# Revit family: d0086212_REVIT-TP96
name_source: partatom
category: Mechanical Equipment
revit_build: Autodesk Revit 2017 (Build: 20190507_1515(x64)
units: mm (PartAtom-declared; Revit-internal decimal feet)

## family parameters
Always vertical = Yes
Cut with Voids When Loaded = Yes
Part Type = Normal
Room Calculation Point = No
Round Connector Dimension = Use Radius
Shared = No
Work Plane-Based = No

## types (50) — shared parameters
Air Inlet Radius = 3 5/16"
Assembly Code = D3020100
Burner Housing Y = 3 13/16"
Burner Nozzle Radius = 2 5/8"
Combustion Air Connection = 6 5/8"
Combustion Air Connection Extension = 5 13/16"
Combustion Air Inlet Radius = 3 5/16"
Condensate Connection = 3/4"
Condensate Drain Extension = 12"
Condensate Location = 4"
Condensate Outlet Extension = 15 1/4"
Condensate Radius = 3/8"
Control Enclosure Height = 38"
Control Enclosure Width = 12"
Cowling Radius = 14 5/8"
Description = TURBOPOWER® 96 ▪ CONDENSING GAS WATER HEATER
Disclaimer = This rendering is for building modeling purposes only. Submittal/catalog is still the contract document. PVI reserves the right to change design and specification without notice.
Drain Angle = 90.00°
Drain Height = 4 3/8"
Economizer Height = 12 3/8"
Flue Collector Insert Radius = 7 9/16"
Flue Collector Outlet Extension = 7 5/8"
Flue Collector Outlet Radius = 3 3/8"
Gas Train Height = 14 7/8"
Gas Train Location = 9 1/4"
Manufacturer = PVI Industries, LLC
Skid Height = 5"
Tank Building Outlet = 18 3/16"
URL = www.pvi.com
Vent Connection = 6 5/8"
Vent Connection Height = 2 3/4"
Vent Enclosure Height = 4"
Vent Radius = 3 5/16"

## per-type parameters (varying)
- 50 L 250A-TPX: 100 Prefix Recovery Rate 40F to 140F (gph)=-; 130 Prefix Recovery Rate 40F to 140F (gph)=-; 160 Prefix Recovery Rate 40F to 140F (gph)=-; 50 Prefix Recovery Rate 40F to 140F (gph)=587; 75 Prefix Recovery Rate 40F to 140F (gph)=-; Building Return Connection Height 50 (250-400gal only) prefix=14 3/16"; Building Return Connection Height 50-160 prefix=10 1/2"; Building Return Extension 250-400gal=35 7/8"; Building Return Extension 500-600gal=5"; Building Return Extension Angle 500-600gal=45.00°; Building Return Height=18 3/16"; Building Return Location=25 3/8"; Building Return NPT=1 1/2"; Building Return Radius=3/4"; Building Return to Economizer=7 5/8"; Burner Conn Height=57 7/8"; Burner Height=18"; Burner Housing -Y=15 5/8"; Burner Housing Extension=19"; Burner Housing to Left=5 3/16"; Burner Housing to Right=7 1/4"; Burner Nozzle Extension=12 3/8"; Cold Inlet Extension=34"; Cold Inlet NPT=2"; Cold Inlet Radius=1"; Combustion Air Connection X=15 7/16"; Combustion Air Connection to Right=3 9/16"; Condensate Extension=4 3/8"; Control Enclosure Angle=56.00°; Control Enclosure Location=41 5/16"; Control Panel Extension=30"; Drain Extension=24 5/8"; Drain NPT=1"; Drain Radius=1/2"; Economizer Connection Y=5"; Economizer Depth=10"; Economizer Inlet Outlet Connection Spacing=4"; Economizer Width=32"; Energy Height=30 7/8"; Flue Collector Extension=8 13/16"; Flue Collector Outlet to Front=3 11/16"; Flue Collector Radius=12 1/8"; Front Cowling Extension=31 1/4"; Gas Inlet NPT=1"; Gas Inlet Radius=1/2"; Gas Train Extension=17 3/8"; Gas Train To Front=10 11/16"; Gas Train Vertical=19 1/8"; Gas Train to Left=4 3/8"; Gas Train to Rear=9 11/16"; Height to Cold Inlet=19 7/16"; Height to Hot Outlet 400-1500gal=45"; Hot Outlet Angle=90.00°; Hot Outlet Extension=24"; Hot Outlet Radius=1"; Hot Outlet Side 400-1500gal NPT=0"; Hot Outlet Side Extension=24"; Hot Outlet Top 250-400gal NPT=2"; Input=500000 Btu/h; Model=50 L 250A-TPX; Pump Extension=27 3/8"; Pump Line Radius=5/8"; Pump Line to Economizer Location=29 3/4"; Rear Cowling Extension=1"; Relief Angle 50-160 Prefix=45.00°; Relief Angle 75-160 Prefix=30.00°; Relief Extension=27"; Relief Extension 50-160 Prefix=27"; Relief Extension 75-160 Prefix=5"; Relief Height=47"; Relief NPT=3/4"; Relief Radius=3/8"; Shipping Weight lbs.=1710; Skid Length=72 1/2"; Skid Spacing=28"; Skid to Front=44 13/16"; Test Building Return Height=16"; Unit Height=62 7/8"; Unit Radius=23"; Vent Connection Housing Extension=8 13/16"; Vent Extension=26 3/8"; Vent Height=7 1/4"; Vent Location=5 3/8"
- 50 L 300A-TPX: 100 Prefix Recovery Rate 40F to 140F (gph)=-; 130 Prefix Recovery Rate 40F to 140F (gph)=-; 160 Prefix Recovery Rate 40F to 140F (gph)=-; 50 Prefix Recovery Rate 40F to 140F (gph)=587; 75 Prefix Recovery Rate 40F to 140F (gph)=-; Building Return Connection Height 50 (250-400gal only) prefix=14 3/16"; Building Return Connection Height 50-160 prefix=10 1/2"; Building Return Extension 250-400gal=35 7/8"; Building Return Extension 500-600gal=5"; Building Return Extension Angle 500-600gal=45.00°; Building Return Height=18 3/16"; Building Return Location=25 3/8"; Building Return NPT=1 1/2"; Building Return Radius=3/4"; Building Return to Economizer=7 5/8"; Burner Conn Height=69 7/8"; Burner Height=18"; Burner Housing -Y=15 5/8"; Burner Housing Extension=19"; Burner Housing to Left=5 3/16"; Burner Housing to Right=7 1/4"; Burner Nozzle Extension=12 3/8"; Cold Inlet Extension=34"; Cold Inlet NPT=2"; Cold Inlet Radius=1"; Combustion Air Connection X=15 7/16"; Combustion Air Connection to Right=3 9/16"; Condensate Extension=4 3/8"; Control Enclosure Angle=56.00°; Control Enclosure Location=51 1/4"; Control Panel Extension=30"; Drain Extension=24 5/8"; Drain NPT=1"; Drain Radius=1/2"; Economizer Connection Y=5"; Economizer Depth=10"; Economizer Inlet Outlet Connection Spacing=4"; Economizer Width=32"; Energy Height=30 7/8"; Flue Collector Extension=8 13/16"; Flue Collector Outlet to Front=3 11/16"; Flue Collector Radius=12 1/8"; Front Cowling Extension=31 1/4"; Gas Inlet NPT=1"; Gas Inlet Radius=1/2"; Gas Train Extension=17 3/8"; Gas Train To Front=10 11/16"; Gas Train Vertical=19 1/8"; Gas Train to Left=4 3/8"; Gas Train to Rear=9 11/16"; Height to Cold Inlet=19 7/16"; Height to Hot Outlet 400-1500gal=57"; Hot Outlet Angle=90.00°; Hot Outlet Extension=24"; Hot Outlet Radius=1"; Hot Outlet Side 400-1500gal NPT=0"; Hot Outlet Side Extension=24"; Hot Outlet Top 250-400gal NPT=2"; Input=500000 Btu/h; Model=50 L 300A-TPX; Pump Extension=27 3/8"; Pump Line Radius=5/8"; Pump Line to Economizer Location=29 3/4"; Rear Cowling Extension=1"; Relief Angle 50-160 Prefix=45.00°; Relief Angle 75-160 Prefix=30.00°; Relief Extension=27"; Relief Extension 50-160 Prefix=27"; Relief Extension 75-160 Prefix=5"; Relief Height=59"; Relief NPT=3/4"; Relief Radius=3/8"; Shipping Weight lbs.=1770; Skid Length=72 1/2"; Skid Spacing=28"; Skid to Front=44 13/16"; Test Building Return Height=16 3/16"; Unit Height=74 7/8"; Unit Radius=23"; Vent Connection Housing Extension=8 13/16"; Vent Extension=26 3/8"; Vent Height=7 1/4"; Vent Location=5 3/8"
- 50 L 400A-TPX: 100 Prefix Recovery Rate 40F to 140F (gph)=-; 130 Prefix Recovery Rate 40F to 140F (gph)=-; 160 Prefix Recovery Rate 40F to 140F (gph)=-; 50 Prefix Recovery Rate 40F to 140F (gph)=587; 75 Prefix Recovery Rate 40F to 140F (gph)=-; Building Return Connection Height 50 (250-400gal only) prefix=14 3/16"; Building Return Connection Height 50-160 prefix=10 1/2"; Building Return Extension 250-400gal=35 7/8"; Building Return Extension 500-600gal=5"; Building Return Extension Angle 500-600gal=45.00°; Building Return Height=18 3/16"; Building Return Location=25 3/8"; Building Return NPT=1 1/2"; Building Return Radius=3/4"; Building Return to Economizer=7 5/8"; Burner Conn Height=81 7/8"; Burner Height=18"; Burner Housing -Y=15 5/8"; Burner Housing Extension=19"; Burner Housing to Left=5 3/16"; Burner Housing to Right=7 1/4"; Burner Nozzle Extension=12 3/8"; Cold Inlet Extension=34"; Cold Inlet NPT=2"; Cold Inlet Radius=1"; Combustion Air Connection X=15 7/16"; Combustion Air Connection to Right=3 9/16"; Condensate Extension=4 3/8"; Control Enclosure Angle=56.00°; Control Enclosure Location=51 1/4"; Control Panel Extension=30"; Drain Extension=24 5/8"; Drain NPT=1"; Drain Radius=1/2"; Economizer Connection Y=5"; Economizer Depth=10"; Economizer Inlet Outlet Connection Spacing=4"; Economizer Width=32"; Energy Height=30 7/8"; Flue Collector Extension=8 13/16"; Flue Collector Outlet to Front=3 11/16"; Flue Collector Radius=12 1/8"; Front Cowling Extension=31 1/4"; Gas Inlet NPT=1"; Gas Inlet Radius=1/2"; Gas Train Extension=17 3/8"; Gas Train To Front=10 11/16"; Gas Train Vertical=19 1/8"; Gas Train to Left=4 3/8"; Gas Train to Rear=9 11/16"; Height to Cold Inlet=19 7/16"; Height to Hot Outlet 400-1500gal=73 1/2"; Hot Outlet Angle=0.00°; Hot Outlet Extension=24"; Hot Outlet Radius=1"; Hot Outlet Side 400-1500gal NPT=0"; Hot Outlet Side Extension=24"; Hot Outlet Top 250-400gal NPT=2"; Input=500000 Btu/h; Model=50 L 400A-TPX; Pump Extension=27 3/8"; Pump Line Radius=5/8"; Pump Line to Economizer Location=29 3/4"; Rear Cowling Extension=1"; Relief Angle 50-160 Prefix=45.00°; Relief Angle 75-160 Prefix=30.00°; Relief Extension=27"; Relief Extension 50-160 Prefix=27"; Relief Extension 75-160 Prefix=5"; Relief Height=71"; Relief NPT=3/4"; Relief Radius=3/8"; Shipping Weight lbs.=1805; Skid Length=72 1/2"; Skid Spacing=28"; Skid to Front=44 13/16"; Test Building Return Height=16 3/16"; Unit Height=86 7/8"; Unit Radius=23"; Vent Connection Housing Extension=8 13/16"; Vent Extension=26 3/8"; Vent Height=7 1/4"; Vent Location=5 3/8"
- 75 L 250A-TPX: 100 Prefix Recovery Rate 40F to 140F (gph)=-; 130 Prefix Recovery Rate 40F to 140F (gph)=-; 160 Prefix Recovery Rate 40F to 140F (gph)=-; 50 Prefix Recovery Rate 40F to 140F (gph)=-; 75 Prefix Recovery Rate 40F to 140F (gph)=881; Building Return Connection Height 50 (250-400gal only) prefix=1/2"; Building Return Connection Height 50-160 prefix=14 3/16"; Building Return Extension 250-400gal=40 3/8"; Building Return Extension 500-600gal=5"; Building Return Extension Angle 500-600gal=45.00°; Building Return Height=18 3/16"; Building Return Location=28 1/2"; Building Return NPT=1 1/2"; Building Return Radius=3/4"; Building Return to Economizer=10 7/16"; Burner Conn Height=57 7/8"; Burner Height=18"; Burner Housing -Y=18 7/16"; Burner Housing Extension=20"; Burner Housing to Left=7 1/8"; Burner Housing to Right=7 7/8"; Burner Nozzle Extension=12 3/8"; Cold Inlet Extension=35 1/2"; Cold Inlet NPT=2"; Cold Inlet Radius=1"; Combustion Air Connection X=15 7/16"; Combustion Air Connection to Right=3 9/16"; Condensate Extension=4 3/8"; Control Enclosure Angle=56.00°; Control Enclosure Location=41 5/16"; Control Panel Extension=30"; Drain Extension=24 5/8"; Drain NPT=1"; Drain Radius=1/2"; Economizer Connection Y=5"; Economizer Depth=10"; Economizer Inlet Outlet Connection Spacing=4"; Economizer Width=32"; Energy Height=30 7/8"; Flue Collector Extension=8 13/16"; Flue Collector Outlet to Front=3 11/16"; Flue Collector Radius=12 1/8"; Front Cowling Extension=37 1/4"; Gas Inlet NPT=1"; Gas Inlet Radius=1/2"; Gas Train Extension=17 3/8"; Gas Train To Front=11 5/8"; Gas Train Vertical=20 5/8"; Gas Train to Left=4 3/8"; Gas Train to Rear=10 11/16"; Height to Cold Inlet=19 7/16"; Height to Hot Outlet 400-1500gal=45"; Hot Outlet Angle=90.00°; Hot Outlet Extension=24"; Hot Outlet Radius=1"; Hot Outlet Side 400-1500gal NPT=0"; Hot Outlet Side Extension=24"; Hot Outlet Top 250-400gal NPT=2"; Input=750000 Btu/h; Model=75 L 250A-TPX; Pump Extension=27 3/8"; Pump Line Radius=5/8"; Pump Line to Economizer Location=31 11/16"; Rear Cowling Extension=1"; Relief Angle 50-160 Prefix=45.00°; Relief Angle 75-160 Prefix=30.00°; Relief Extension=27"; Relief Extension 50-160 Prefix=27"; Relief Extension 75-160 Prefix=29"; Relief Height=47"; Relief NPT=3/4"; Relief Radius=3/8"; Shipping Weight lbs.=1830; Skid Length=78 3/4"; Skid Spacing=28"; Skid to Front=51 1/16"; Test Building Return Height=16 3/16"; Unit Height=62 7/8"; Unit Radius=23"; Vent Connection Housing Extension=8 13/16"; Vent Extension=26 3/8"; Vent Height=7 1/4"; Vent Location=5 3/8"
- 75 L 300A-TPX: 100 Prefix Recovery Rate 40F to 140F (gph)=-; 130 Prefix Recovery Rate 40F to 140F (gph)=-; 160 Prefix Recovery Rate 40F to 140F (gph)=-; 50 Prefix Recovery Rate 40F to 140F (gph)=-; 75 Prefix Recovery Rate 40F to 140F (gph)=881; Building Return Connection Height 50 (250-400gal only) prefix=1/2"; Building Return Connection Height 50-160 prefix=14 3/16"; Building Return Extension 250-400gal=40 3/8"; Building Return Extension 500-600gal=5"; Building Return Extension Angle 500-600gal=45.00°; Building Return Height=18 3/16"; Building Return Location=28 1/2"; Building Return NPT=1 1/2"; Building Return Radius=3/4"; Building Return to Economizer=10 7/16"; Burner Conn Height=69 7/8"; Burner Height=18"; Burner Housing -Y=18 7/16"; Burner Housing Extension=20"; Burner Housing to Left=7 1/8"; Burner Housing to Right=7 7/8"; Burner Nozzle Extension=12 3/8"; Cold Inlet Extension=35 1/2"; Cold Inlet NPT=2"; Cold Inlet Radius=1"; Combustion Air Connection X=15 7/16"; Combustion Air Connection to Right=3 9/16"; Condensate Extension=4 3/8"; Control Enclosure Angle=56.00°; Control Enclosure Location=51 1/4"; Control Panel Extension=30"; Drain Extension=24 5/8"; Drain NPT=1"; Drain Radius=1/2"; Economizer Connection Y=5"; Economizer Depth=10"; Economizer Inlet Outlet Connection Spacing=4"; Economizer Width=32"; Energy Height=30 7/8"; Flue Collector Extension=8 13/16"; Flue Collector Outlet to Front=3 11/16"; Flue Collector Radius=12 1/8"; Front Cowling Extension=37 1/4"; Gas Inlet NPT=1"; Gas Inlet Radius=1/2"; Gas Train Extension=17 3/8"; Gas Train To Front=11 5/8"; Gas Train Vertical=20 5/8"; Gas Train to Left=4 3/8"; Gas Train to Rear=10 11/16"; Height to Cold Inlet=19 7/16"; Height to Hot Outlet 400-1500gal=57"; Hot Outlet Angle=90.00°; Hot Outlet Extension=24"; Hot Outlet Radius=1"; Hot Outlet Side 400-1500gal NPT=0"; Hot Outlet Side Extension=24"; Hot Outlet Top 250-400gal NPT=2"; Input=750000 Btu/h; Model=75 L 300A-TPX; Pump Extension=27 3/8"; Pump Line Radius=5/8"; Pump Line to Economizer Location=31 11/16"; Rear Cowling Extension=1"; Relief Angle 50-160 Prefix=45.00°; Relief Angle 75-160 Prefix=30.00°; Relief Extension=27"; Relief Extension 50-160 Prefix=27"; Relief Extension 75-160 Prefix=29"; Relief Height=59"; Relief NPT=3/4"; Relief Radius=3/8"; Shipping Weight lbs.=1850; Skid Length=78 3/4"; Skid Spacing=28"; Skid to Front=51 1/16"; Test Building Return Height=16 3/16"; Unit Height=74 7/8"; Unit Radius=23"; Vent Connection Housing Extension=8 13/16"; Vent Extension=26 3/8"; Vent Height=7 1/4"; Vent Location=5 3/8"
- 75 L 400A-TPX: 100 Prefix Recovery Rate 40F to 140F (gph)=-; 130 Prefix Recovery Rate 40F to 140F (gph)=-; 160 Prefix Recovery Rate 40F to 140F (gph)=-; 50 Prefix Recovery Rate 40F to 140F (gph)=-; 75 Prefix Recovery Rate 40F to 140F (gph)=881; Building Return Connection Height 50 (250-400gal only) prefix=1/2"; Building Return Connection Height 50-160 prefix=14 3/16"; Building Return Extension 250-400gal=40 3/8"; Building Return Extension 500-600gal=5"; Building Return Extension Angle 500-600gal=45.00°; Building Return Height=18 3/16"; Building Return Location=28 1/2"; Building Return NPT=1 1/2"; Building Return Radius=3/4"; Building Return to Economizer=10 7/16"; Burner Conn Height=81 7/8"; Burner Height=18"; Burner Housing -Y=18 7/16"; Burner Housing Extension=20"; Burner Housing to Left=7 1/8"; Burner Housing to Right=7 7/8"; Burner Nozzle Extension=12 3/8"; Cold Inlet Extension=35 1/2"; Cold Inlet NPT=2"; Cold Inlet Radius=1"; Combustion Air Connection X=15 7/16"; Combustion Air Connection to Right=3 9/16"; Condensate Extension=4 3/8"; Control Enclosure Angle=56.00°; Control Enclosure Location=51 1/4"; Control Panel Extension=30"; Drain Extension=24 5/8"; Drain NPT=1"; Drain Radius=1/2"; Economizer Connection Y=5"; Economizer Depth=10"; Economizer Inlet Outlet Connection Spacing=4"; Economizer Width=32"; Energy Height=30 7/8"; Flue Collector Extension=8 13/16"; Flue Collector Outlet to Front=3 11/16"; Flue Collector Radius=12 1/8"; Front Cowling Extension=37 1/4"; Gas Inlet NPT=1"; Gas Inlet Radius=1/2"; Gas Train Extension=17 3/8"; Gas Train To Front=11 5/8"; Gas Train Vertical=20 5/8"; Gas Train to Left=4 3/8"; Gas Train to Rear=10 11/16"; Height to Cold Inlet=19 7/16"; Height to Hot Outlet 400-1500gal=73 1/2"; Hot Outlet Angle=0.00°; Hot Outlet Extension=24"; Hot Outlet Radius=1"; Hot Outlet Side 400-1500gal NPT=0"; Hot Outlet Side Extension=24"; Hot Outlet Top 250-400gal NPT=2"; Input=750000 Btu/h; Model=75 L 400A-TPX; Pump Extension=27 3/8"; Pump Line Radius=5/8"; Pump Line to Economizer Location=31 11/16"; Rear Cowling Extension=1"; Relief Angle 50-160 Prefix=45.00°; Relief Angle 75-160 Prefix=30.00°; Relief Extension=27"; Relief Extension 50-160 Prefix=27"; Relief Extension 75-160 Prefix=29"; Relief Height=71"; Relief NPT=3/4"; Relief Radius=3/8"; Shipping Weight lbs.=1885; Skid Length=78 3/4"; Skid Spacing=28"; Skid to Front=51 1/16"; Test Building Return Height=16 3/16"; Unit Height=86 7/8"; Unit Radius=23"; Vent Connection Housing Extension=8 13/16"; Vent Extension=26 3/8"; Vent Height=7 1/4"; Vent Location=5 3/8"
- 130 L 250A-TPX: 100 Prefix Recovery Rate 40F to 140F (gph)=-; 130 Prefix Recovery Rate 40F to 140F (gph)=1527; 160 Prefix Recovery Rate 40F to 140F (gph)=-; 50 Prefix Recovery Rate 40F to 140F (gph)=-; 75 Prefix Recovery Rate 40F to 140F (gph)=-; Building Return Connection Height 50 (250-400gal only) prefix=1/2"; Building Return Connection Height 50-160 prefix=14 1/2"; Building Return Extension 250-400gal=35 7/8"; Building Return Extension 500-600gal=5"; Building Return Extension Angle 500-600gal=45.00°; Building Return Height=18 3/16"; Building Return Location=25 3/8"; Building Return NPT=2"; Building Return Radius=1"; Building Return to Economizer=17"; Burner Conn Height=57 7/8"; Burner Height=18"; Burner Housing -Y=23 1/8"; Burner Housing Extension=24 1/4"; Burner Housing to Left=7 1/4"; Burner Housing to Right=11 1/2"; Burner Nozzle Extension=16 7/16"; Cold Inlet Extension=35 3/8"; Cold Inlet NPT=2"; Cold Inlet Radius=1"; Combustion Air Connection X=20"; Combustion Air Connection to Right=6 7/8"; Condensate Extension=4 3/8"; Control Enclosure Angle=56.00°; Control Enclosure Location=41 5/16"; Control Panel Extension=30"; Drain Extension=24 5/8"; Drain NPT=1"; Drain Radius=1/2"; Economizer Connection Y=5"; Economizer Depth=18"; Economizer Inlet Outlet Connection Spacing=7"; Economizer Width=32 3/4"; Energy Height=30 7/8"; Flue Collector Extension=13 1/8"; Flue Collector Outlet to Front=6 5/8"; Flue Collector Radius=12 1/8"; Front Cowling Extension=39 1/4"; Gas Inlet NPT=1 1/2"; Gas Inlet Radius=3/4"; Gas Train Extension=19 3/8"; Gas Train To Front=11 5/8"; Gas Train Vertical=24"; Gas Train to Left=6 5/8"; Gas Train to Rear=10 11/16"; Height to Cold Inlet=19 7/16"; Height to Hot Outlet 400-1500gal=45"; Hot Outlet Angle=90.00°; Hot Outlet Extension=24"; Hot Outlet Radius=1"; Hot Outlet Side 400-1500gal NPT=0"; Hot Outlet Side Extension=24"; Hot Outlet Top 250-400gal NPT=2"; Input=1300000 Btu/h; Model=130 L 250A-TPX; Pump Extension=27 3/8"; Pump Line Radius=1"; Pump Line to Economizer Location=31"; Rear Cowling Extension=43 5/16"; Relief Angle 50-160 Prefix=45.00°; Relief Angle 75-160 Prefix=30.00°; Relief Extension=27"; Relief Extension 50-160 Prefix=27"; Relief Extension 75-160 Prefix=29"; Relief Height=47"; Relief NPT=3/4"; Relief Radius=3/8"; Shipping Weight lbs.=2165; Skid Length=90 3/16"; Skid Spacing=28"; Skid to Front=60 7/8"; Test Building Return Height=16 3/16"; Unit Height=62 7/8"; Unit Radius=23"; Vent Connection Housing Extension=8 13/16"; Vent Extension=26 3/8"; Vent Height=7 1/4"; Vent Location=5 3/8"
- 130 L 300A-TPX: 100 Prefix Recovery Rate 40F to 140F (gph)=-; 130 Prefix Recovery Rate 40F to 140F (gph)=1527; 160 Prefix Recovery Rate 40F to 140F (gph)=-; 50 Prefix Recovery Rate 40F to 140F (gph)=-; 75 Prefix Recovery Rate 40F to 140F (gph)=-; Building Return Connection Height 50 (250-400gal only) prefix=1/2"; Building Return Connection Height 50-160 prefix=14 1/2"; Building Return Extension 250-400gal=35 7/8"; Building Return Extension 500-600gal=5"; Building Return Extension Angle 500-600gal=45.00°; Building Return Height=18 3/16"; Building Return Location=25 3/8"; Building Return NPT=2"; Building Return Radius=1"; Building Return to Economizer=17"; Burner Conn Height=69 7/8"; Burner Height=18"; Burner Housing -Y=23 1/8"; Burner Housing Extension=24 1/4"; Burner Housing to Left=7 1/4"; Burner Housing to Right=11 1/2"; Burner Nozzle Extension=16 7/16"; Cold Inlet Extension=35 3/8"; Cold Inlet NPT=2"; Cold Inlet Radius=1"; Combustion Air Connection X=20"; Combustion Air Connection to Right=6 7/8"; Condensate Extension=4 3/8"; Control Enclosure Angle=56.00°; Control Enclosure Location=51 1/4"; Control Panel Extension=30"; Drain Extension=24 5/8"; Drain NPT=1"; Drain Radius=1/2"; Economizer Connection Y=5"; Economizer Depth=18"; Economizer Inlet Outlet Connection Spacing=7"; Economizer Width=32 3/4"; Energy Height=30 7/8"; Flue Collector Extension=13 1/8"; Flue Collector Outlet to Front=6 5/8"; Flue Collector Radius=12 1/8"; Front Cowling Extension=39 1/4"; Gas Inlet NPT=1 1/2"; Gas Inlet Radius=3/4"; Gas Train Extension=19 3/8"; Gas Train To Front=11 5/8"; Gas Train Vertical=24"; Gas Train to Left=6 5/8"; Gas Train to Rear=10 11/16"; Height to Cold Inlet=19 7/16"; Height to Hot Outlet 400-1500gal=57"; Hot Outlet Angle=90.00°; Hot Outlet Extension=24"; Hot Outlet Radius=1"; Hot Outlet Side 400-1500gal NPT=0"; Hot Outlet Side Extension=24"; Hot Outlet Top 250-400gal NPT=2"; Input=1300000 Btu/h; Model=130 L 300A-TPX; Pump Extension=27 3/8"; Pump Line Radius=1"; Pump Line to Economizer Location=31"; Rear Cowling Extension=43 5/16"; Relief Angle 50-160 Prefix=45.00°; Relief Angle 75-160 Prefix=30.00°; Relief Extension=27"; Relief Extension 50-160 Prefix=27"; Relief Extension 75-160 Prefix=29"; Relief Height=59"; Relief NPT=3/4"; Relief Radius=3/8"; Shipping Weight lbs.=2120; Skid Length=90 3/16"; Skid Spacing=28"; Skid to Front=60 7/8"; Test Building Return Height=16 3/16"; Unit Height=74 7/8"; Unit Radius=23"; Vent Connection Housing Extension=8 13/16"; Vent Extension=26 3/8"; Vent Height=7 1/4"; Vent Location=5 3/8"
- 130 L 400A-TPX: 100 Prefix Recovery Rate 40F to 140F (gph)=-; 130 Prefix Recovery Rate 40F to 140F (gph)=1527; 160 Prefix Recovery Rate 40F to 140F (gph)=-; 50 Prefix Recovery Rate 40F to 140F (gph)=-; 75 Prefix Recovery Rate 40F to 140F (gph)=-; Building Return Connection Height 50 (250-400gal only) prefix=1/2"; Building Return Connection Height 50-160 prefix=14 1/2"; Building Return Extension 250-400gal=35 7/8"; Building Return Extension 500-600gal=5"; Building Return Extension Angle 500-600gal=45.00°; Building Return Height=18 3/16"; Building Return Location=25 3/8"; Building Return NPT=2"; Building Return Radius=1"; Building Return to Economizer=17"; Burner Conn Height=81 7/8"; Burner Height=18"; Burner Housing -Y=23 1/8"; Burner Housing Extension=24 1/4"; Burner Housing to Left=7 1/4"; Burner Housing to Right=11 1/2"; Burner Nozzle Extension=16 7/16"; Cold Inlet Extension=35 3/8"; Cold Inlet NPT=2"; Cold Inlet Radius=1"; Combustion Air Connection X=20"; Combustion Air Connection to Right=6 7/8"; Condensate Extension=4 3/8"; Control Enclosure Angle=56.00°; Control Enclosure Location=51 1/4"; Control Panel Extension=30"; Drain Extension=24 5/8"; Drain NPT=1"; Drain Radius=1/2"; Economizer Connection Y=5"; Economizer Depth=18"; Economizer Inlet Outlet Connection Spacing=7"; Economizer Width=32 3/4"; Energy Height=30 7/8"; Flue Collector Extension=13 3/16"; Flue Collector Outlet to Front=6 5/8"; Flue Collector Radius=12 1/8"; Front Cowling Extension=39 1/4"; Gas Inlet NPT=1 1/2"; Gas Inlet Radius=3/4"; Gas Train Extension=19 3/8"; Gas Train To Front=11 5/8"; Gas Train Vertical=24"; Gas Train to Left=6 5/8"; Gas Train to Rear=10 11/16"; Height to Cold Inlet=19 7/16"; Height to Hot Outlet 400-1500gal=73 1/2"; Hot Outlet Angle=0.00°; Hot Outlet Extension=24"; Hot Outlet Radius=1"; Hot Outlet Side 400-1500gal NPT=0"; Hot Outlet Side Extension=24"; Hot Outlet Top 250-400gal NPT=2"; Input=1300000 Btu/h; Model=130 L 400A-TPX; Pump Extension=27 3/8"; Pump Line Radius=1"; Pump Line to Economizer Location=31"; Rear Cowling Extension=43 5/16"; Relief Angle 50-160 Prefix=45.00°; Relief Angle 75-160 Prefix=35.00°; Relief Extension=27"; Relief Extension 50-160 Prefix=27"; Relief Extension 75-160 Prefix=29"; Relief Height=71"; Relief NPT=3/4"; Relief Radius=3/8"; Shipping Weight lbs.=2155; Skid Length=90 3/16"; Skid Spacing=28"; Skid to Front=60 7/8"; Test Building Return Height=16 3/16"; Unit Height=86 7/8"; Unit Radius=23"; Vent Connection Housing Extension=8 13/16"; Vent Extension=26 3/8"; Vent Height=7 1/4"; Vent Location=5 3/8"
- 50 L 500A-TPX: 100 Prefix Recovery Rate 40F to 140F (gph)=-; 130 Prefix Recovery Rate 40F to 140F (gph)=-; 160 Prefix Recovery Rate 40F to 140F (gph)=-; 50 Prefix Recovery Rate 40F to 140F (gph)=587; 75 Prefix Recovery Rate 40F to 140F (gph)=-; Building Return Connection Height 50 (250-400gal only) prefix=1/2"; Building Return Connection Height 50-160 prefix=14 3/8"; Building Return Extension 250-400gal=1"; Building Return Extension 500-600gal=35 25/32"; Building Return Extension Angle 500-600gal=35.00°; Building Return Height=18 3/8"; Building Return Location=29 3/16"; Building Return NPT=1 1/2"; Building Return Radius=3/4"; Building Return to Economizer=17 9/16"; Burner Conn Height=71"; Burner Height=18"; Burner Housing -Y=15 5/8"; Burner Housing Extension=19"; Burner Housing to Left=5 3/16"; Burner Housing to Right=7 1/4"; Burner Nozzle Extension=12 3/8"; Cold Inlet Extension=34 3/4"; Cold Inlet NPT=3"; Cold Inlet Radius=1 1/2"; Combustion Air Connection X=15 7/16"; Combustion Air Connection to Right=3 9/16"; Condensate Extension=4 3/8"; Control Enclosure Angle=45.00°; Control Enclosure Location=41 5/16"; Control Panel Extension=35"; Drain Extension=29 5/8"; Drain NPT=1 1/2"; Drain Radius=3/4"; Economizer Connection Y=5"; Economizer Depth=10"; Economizer Inlet Outlet Connection Spacing=4"; Economizer Width=32"; Energy Height=30 7/8"; Flue Collector Extension=8 13/16"; Flue Collector Outlet to Front=3 11/16"; Flue Collector Radius=12 1/8"; Front Cowling Extension=36 1/4"; Gas Inlet NPT=1"; Gas Inlet Radius=1/2"; Gas Train Extension=17 3/8"; Gas Train To Front=10 11/16"; Gas Train Vertical=19 1/8"; Gas Train to Left=4 3/8"; Gas Train to Rear=9 11/16"; Height to Cold Inlet=19 7/16"; Height to Hot Outlet 400-1500gal=62 1/2"; Hot Outlet Angle=0.00°; Hot Outlet Extension=29"; Hot Outlet Radius=1 1/2"; Hot Outlet Side 400-1500gal NPT=0"; Hot Outlet Side Extension=29"; Hot Outlet Top 250-400gal NPT=3"; Input=500000 Btu/h; Model=50 L 500A-TPX; Pump Extension=32 3/8"; Pump Line Radius=5/8"; Pump Line to Economizer Location=32 1/2"; Rear Cowling Extension=1"; Relief Angle 50-160 Prefix=35.00°; Relief Angle 75-160 Prefix=12.00°; Relief Extension=32"; Relief Extension 50-160 Prefix=32"; Relief Extension 75-160 Prefix=5"; Relief Height=60 1/8"; Relief NPT=3/4"; Relief Radius=3/8"; Shipping Weight lbs.=2195; Skid Length=82 7/8"; Skid Spacing=28"; Skid to Front=49 7/8"; Test Building Return Height=16 3/16"; Unit Height=76"; Unit Radius=28"; Vent Connection Housing Extension=8 13/16"; Vent Extension=31 3/8"; Vent Height=7 1/4"; Vent Location=5 3/8"
- 50 L 600A-TPX: 100 Prefix Recovery Rate 40F to 140F (gph)=-; 130 Prefix Recovery Rate 40F to 140F (gph)=-; 160 Prefix Recovery Rate 40F to 140F (gph)=-; 50 Prefix Recovery Rate 40F to 140F (gph)=587; 75 Prefix Recovery Rate 40F to 140F (gph)=-; Building Return Connection Height 50 (250-400gal only) prefix=1/2"; Building Return Connection Height 50-160 prefix=14 3/8"; Building Return Extension 250-400gal=1"; Building Return Extension 500-600gal=35 25/32"; Building Return Extension Angle 500-600gal=35.00°; Building Return Height=18 3/8"; Building Return Location=29 3/16"; Building Return NPT=1 1/2"; Building Return Radius=3/4"; Building Return to Economizer=17 9/16"; Burner Conn Height=83 5/8"; Burner Height=18"; Burner Housing -Y=15 5/8"; Burner Housing Extension=19"; Burner Housing to Left=5 3/16"; Burner Housing to Right=7 1/4"; Burner Nozzle Extension=12 3/8"; Cold Inlet Extension=34 3/4"; Cold Inlet NPT=3"; Cold Inlet Radius=1 1/2"; Combustion Air Connection X=15 7/16"; Combustion Air Connection to Right=3 9/16"; Condensate Extension=4 3/8"; Control Enclosure Angle=45.00°; Control Enclosure Location=41 5/16"; Control Panel Extension=35"; Drain Extension=29 5/8"; Drain NPT=1 1/2"; Drain Radius=3/4"; Economizer Connection Y=5"; Economizer Depth=10"; Economizer Inlet Outlet Connection Spacing=4"; Economizer Width=32"; Energy Height=30 7/8"; Flue Collector Extension=8 13/16"; Flue Collector Outlet to Front=3 11/16"; Flue Collector Radius=12 1/8"; Front Cowling Extension=36 1/4"; Gas Inlet NPT=1"; Gas Inlet Radius=1/2"; Gas Train Extension=17 3/8"; Gas Train To Front=10 11/16"; Gas Train Vertical=19 1/8"; Gas Train to Left=4 3/8"; Gas Train to Rear=9 11/16"; Height to Cold Inlet=19 7/16"; Height to Hot Outlet 400-1500gal=74 1/2"; Hot Outlet Angle=0.00°; Hot Outlet Extension=29"; Hot Outlet Radius=1 1/2"; Hot Outlet Side 400-1500gal NPT=0"; Hot Outlet Side Extension=29"; Hot Outlet Top 250-400gal NPT=3"; Input=500000 Btu/h; Model=50 L 600A-TPX; Pump Extension=32 3/8"; Pump Line Radius=5/8"; Pump Line to Economizer Location=32 1/2"; Rear Cowling Extension=1"; Relief Angle 50-160 Prefix=35.00°; Relief Angle 75-160 Prefix=12.00°; Relief Extension=32"; Relief Extension 50-160 Prefix=32"; Relief Extension 75-160 Prefix=5"; Relief Height=72 3/4"; Relief NPT=3/4"; Relief Radius=3/8"; Shipping Weight lbs.=2430; Skid Length=82 7/8"; Skid Spacing=28"; Skid to Front=49 7/8"; Test Building Return Height=16 3/16"; Unit Height=88 5/8"; Unit Radius=28"; Vent Connection Housing Extension=8 13/16"; Vent Extension=31 3/8"; Vent Height=7 1/4"; Vent Location=5 3/8"
- 75 L 500A-TPX: 100 Prefix Recovery Rate 40F to 140F (gph)=-; 130 Prefix Recovery Rate 40F to 140F (gph)=-; 160 Prefix Recovery Rate 40F to 140F (gph)=-; 50 Prefix Recovery Rate 40F to 140F (gph)=-; 75 Prefix Recovery Rate 40F to 140F (gph)=881; Building Return Connection Height 50 (250-400gal only) prefix=1/2"; Building Return Connection Height 50-160 prefix=14 3/8"; Building Return Extension 250-400gal=1"; Building Return Extension 500-600gal=35 25/32"; Building Return Extension Angle 500-600gal=35.00°; Building Return Height=18 3/8"; Building Return Location=29 3/16"; Building Return NPT=1 1/2"; Building Return Radius=3/4"; Building Return to Economizer=17 9/16"; Burner Conn Height=71"; Burner Height=18"; Burner Housing -Y=18 7/16"; Burner Housing Extension=20"; Burner Housing to Left=7 1/8"; Burner Housing to Right=7 7/8"; Burner Nozzle Extension=12 3/8"; Cold Inlet Extension=34 3/4"; Cold Inlet NPT=3"; Cold Inlet Radius=1 1/2"; Combustion Air Connection X=15 7/16"; Combustion Air Connection to Right=3 9/16"; Condensate Extension=4 3/8"; Control Enclosure Angle=45.00°; Control Enclosure Location=41 5/16"; Control Panel Extension=35"; Drain Extension=29 5/8"; Drain NPT=1 1/2"; Drain Radius=3/4"; Economizer Connection Y=5"; Economizer Depth=10"; Economizer Inlet Outlet Connection Spacing=4"; Economizer Width=32"; Energy Height=30 7/8"; Flue Collector Extension=8 13/16"; Flue Collector Outlet to Front=3 11/16"; Flue Collector Radius=12 1/8"; Front Cowling Extension=36 1/4"; Gas Inlet NPT=1"; Gas Inlet Radius=1/2"; Gas Train Extension=17 3/8"; Gas Train To Front=10 11/16"; Gas Train Vertical=20 5/8"; Gas Train to Left=4 3/8"; Gas Train to Rear=9 11/16"; Height to Cold Inlet=19 7/16"; Height to Hot Outlet 400-1500gal=62 1/2"; Hot Outlet Angle=0.00°; Hot Outlet Extension=29"; Hot Outlet Radius=1 1/2"; Hot Outlet Side 400-1500gal NPT=0"; Hot Outlet Side Extension=29"; Hot Outlet Top 250-400gal NPT=3"; Input=750000 Btu/h; Model=75 L 500A-TPX; Pump Extension=32 3/8"; Pump Line Radius=5/8"; Pump Line to Economizer Location=32 1/2"; Rear Cowling Extension=1"; Relief Angle 50-160 Prefix=35.00°; Relief Angle 75-160 Prefix=27.00°; Relief Extension=32"; Relief Extension 50-160 Prefix=32"; Relief Extension 75-160 Prefix=34"; Relief Height=60 1/8"; Relief NPT=3/4"; Relief Radius=3/8"; Shipping Weight lbs.=2275; Skid Length=82 7/8"; Skid Spacing=28"; Skid to Front=49 7/8"; Test Building Return Height=16 3/16"; Unit Height=76"; Unit Radius=28"; Vent Connection Housing Extension=8 13/16"; Vent Extension=31 3/8"; Vent Height=7 1/4"; Vent Location=5 3/8"
- 75 L 600A-TPX: 100 Prefix Recovery Rate 40F to 140F (gph)=-; 130 Prefix Recovery Rate 40F to 140F (gph)=-; 160 Prefix Recovery Rate 40F to 140F (gph)=-; 50 Prefix Recovery Rate 40F to 140F (gph)=-; 75 Prefix Recovery Rate 40F to 140F (gph)=881; Building Return Connection Height 50 (250-400gal only) prefix=1/2"; Building Return Connection Height 50-160 prefix=14 3/8"; Building Return Extension 250-400gal=1"; Building Return Extension 500-600gal=35 25/32"; Building Return Extension Angle 500-600gal=35.00°; Building Return Height=20"; Building Return Location=29 3/16"; Building Return NPT=1 1/2"; Building Return Radius=3/4"; Building Return to Economizer=17 9/16"; Burner Conn Height=83 5/8"; Burner Height=18"; Burner Housing -Y=18 7/16"; Burner Housing Extension=20"; Burner Housing to Left=7 1/8"; Burner Housing to Right=7 7/8"; Burner Nozzle Extension=12 3/8"; Cold Inlet Extension=34 3/4"; Cold Inlet NPT=3"; Cold Inlet Radius=1 1/2"; Combustion Air Connection X=15 7/16"; Combustion Air Connection to Right=3 9/16"; Condensate Extension=4 3/8"; Control Enclosure Angle=45.00°; Control Enclosure Location=41 5/16"; Control Panel Extension=35"; Drain Extension=29 5/8"; Drain NPT=1 1/2"; Drain Radius=3/4"; Economizer Connection Y=5"; Economizer Depth=10"; Economizer Inlet Outlet Connection Spacing=4"; Economizer Width=32"; Energy Height=30 7/8"; Flue Collector Extension=8 13/16"; Flue Collector Outlet to Front=3 11/16"; Flue Collector Radius=12 1/8"; Front Cowling Extension=36 1/4"; Gas Inlet NPT=1"; Gas Inlet Radius=1/2"; Gas Train Extension=17 3/8"; Gas Train To Front=10 11/16"; Gas Train Vertical=20 5/8"; Gas Train to Left=4 3/8"; Gas Train to Rear=9 11/16"; Height to Cold Inlet=19 7/16"; Height to Hot Outlet 400-1500gal=74 1/2"; Hot Outlet Angle=0.00°; Hot Outlet Extension=29"; Hot Outlet Radius=1 1/2"; Hot Outlet Side 400-1500gal NPT=0"; Hot Outlet Side Extension=29"; Hot Outlet Top 250-400gal NPT=3"; Input=750000 Btu/h; Model=75 L 600A-TPX; Pump Extension=32 3/8"; Pump Line Radius=5/8"; Pump Line to Economizer Location=32 1/2"; Rear Cowling Extension=1"; Relief Angle 50-160 Prefix=35.00°; Relief Angle 75-160 Prefix=27.00°; Relief Extension=32"; Relief Extension 50-160 Prefix=32"; Relief Extension 75-160 Prefix=34"; Relief Height=72 3/4"; Relief NPT=3/4"; Relief Radius=3/8"; Shipping Weight lbs.=2510; Skid Length=82 7/8"; Skid Spacing=28"; Skid to Front=49 7/8"; Test Building Return Height=16 3/16"; Unit Height=88 5/8"; Unit Radius=28"; Vent Connection Housing Extension=8 13/16"; Vent Extension=31 3/8"; Vent Height=7 1/4"; Vent Location=5 3/8"
- 130 L 500A-TPX: 100 Prefix Recovery Rate 40F to 140F (gph)=-; 130 Prefix Recovery Rate 40F to 140F (gph)=1527; 160 Prefix Recovery Rate 40F to 140F (gph)=-; 50 Prefix Recovery Rate 40F to 140F (gph)=-; 75 Prefix Recovery Rate 40F to 140F (gph)=-; Building Return Connection Height 50 (250-400gal only) prefix=1/2"; Building Return Connection Height 50-160 prefix=14 3/8"; Building Return Extension 250-400gal=1"; Building Return Extension 500-600gal=35 25/32"; Building Return Extension Angle 500-600gal=34.75°; Building Return Height=18 3/8"; Building Return Location=29 3/16"; Building Return NPT=2"; Building Return Radius=1"; Building Return to Economizer=31"; Burner Conn Height=71"; Burner Height=18"; Burner Housing -Y=19 7/16"; Burner Housing Extension=24 1/4"; Burner Housing to Left=7 1/4"; Burner Housing to Right=11 1/2"; Burner Nozzle Extension=16 7/16"; Cold Inlet Extension=35 1/4"; Cold Inlet NPT=3"; Cold Inlet Radius=1 1/2"; Combustion Air Connection X=20"; Combustion Air Connection to Right=6 7/8"; Condensate Extension=4 3/16"; Control Enclosure Angle=45.00°; Control Enclosure Location=41 5/16"; Control Panel Extension=35"; Drain Extension=29 5/8"; Drain NPT=1 1/2"; Drain Radius=3/4"; Economizer Connection Y=5"; Economizer Depth=18"; Economizer Inlet Outlet Connection Spacing=7"; Economizer Width=32 3/4"; Energy Height=30 7/8"; Flue Collector Extension=13 1/8"; Flue Collector Outlet to Front=6 5/8"; Flue Collector Radius=11 13/16"; Front Cowling Extension=48 3/16"; Gas Inlet NPT=1"; Gas Inlet Radius=1/2"; Gas Train Extension=19 3/8"; Gas Train To Front=11 5/8"; Gas Train Vertical=24"; Gas Train to Left=6 5/8"; Gas Train to Rear=10 11/16"; Height to Cold Inlet=19 1/8"; Height to Hot Outlet 400-1500gal=62 1/2"; Hot Outlet Angle=0.00°; Hot Outlet Extension=29"; Hot Outlet Radius=1 1/2"; Hot Outlet Side 400-1500gal NPT=0"; Hot Outlet Side Extension=29"; Hot Outlet Top 250-400gal NPT=3"; Input=1300000 Btu/h; Model=130 L 500A-TPX; Pump Extension=32 3/8"; Pump Line Radius=1"; Pump Line to Economizer Location=32 13/16"; Rear Cowling Extension=33 5/8"; Relief Angle 50-160 Prefix=35.00°; Relief Angle 75-160 Prefix=27.00°; Relief Extension=32"; Relief Extension 50-160 Prefix=32"; Relief Extension 75-160 Prefix=34"; Relief Height=60 1/8"; Relief NPT=3/4"; Relief Radius=3/8"; Shipping Weight lbs.=2545; Skid Length=102 1/8"; Skid Spacing=28"; Skid to Front=69 1/8"; Test Building Return Height=16 3/16"; Unit Height=76"; Unit Radius=28"; Vent Connection Housing Extension=8 3/8"; Vent Extension=31 3/8"; Vent Height=7 1/4"; Vent Location=4 11/16"
- 130 L 600A-TPX: 100 Prefix Recovery Rate 40F to 140F (gph)=-; 130 Prefix Recovery Rate 40F to 140F (gph)=1527; 160 Prefix Recovery Rate 40F to 140F (gph)=-; 50 Prefix Recovery Rate 40F to 140F (gph)=-; 75 Prefix Recovery Rate 40F to 140F (gph)=-; Building Return Connection Height 50 (250-400gal only) prefix=1/2"; Building Return Connection Height 50-160 prefix=14 3/8"; Building Return Extension 250-400gal=1"; Building Return Extension 500-600gal=35 25/32"; Building Return Extension Angle 500-600gal=34.75°; Building Return Height=18 3/8"; Building Return Location=29 3/16"; Building Return NPT=2"; Building Return Radius=1"; Building Return to Economizer=31"; Burner Conn Height=83"; Burner Height=18"; Burner Housing -Y=19 7/16"; Burner Housing Extension=24 1/4"; Burner Housing to Left=7 1/4"; Burner Housing to Right=11 1/2"; Burner Nozzle Extension=16 7/16"; Cold Inlet Extension=35 1/4"; Cold Inlet NPT=3"; Cold Inlet Radius=1 1/2"; Combustion Air Connection X=20"; Combustion Air Connection to Right=6 7/8"; Condensate Extension=4 3/16"; Control Enclosure Angle=45.00°; Control Enclosure Location=41 5/16"; Control Panel Extension=35"; Drain Extension=29 5/8"; Drain NPT=1 1/2"; Drain Radius=3/4"; Economizer Connection Y=5"; Economizer Depth=18"; Economizer Inlet Outlet Connection Spacing=7"; Economizer Width=32 3/4"; Energy Height=30 7/8"; Flue Collector Extension=13 3/16"; Flue Collector Outlet to Front=6 5/8"; Flue Collector Radius=11 13/16"; Front Cowling Extension=48 3/16"; Gas Inlet NPT=1"; Gas Inlet Radius=1/2"; Gas Train Extension=19 3/8"; Gas Train To Front=11 5/8"; Gas Train Vertical=24"; Gas Train to Left=6 5/8"; Gas Train to Rear=10 11/16"; Height to Cold Inlet=19 1/8"; Height to Hot Outlet 400-1500gal=74 1/2"; Hot Outlet Angle=0.00°; Hot Outlet Extension=29"; Hot Outlet Radius=1 1/2"; Hot Outlet Side 400-1500gal NPT=0"; Hot Outlet Side Extension=29"; Hot Outlet Top 250-400gal NPT=3"; Input=1300000 Btu/h; Model=130 L 600A-TPX; Pump Extension=32 3/8"; Pump Line Radius=1"; Pump Line to Economizer Location=32 13/16"; Rear Cowling Extension=33 5/8"; Relief Angle 50-160 Prefix=35.00°; Relief Angle 75-160 Prefix=27.00°; Relief Extension=32"; Relief Extension 50-160 Prefix=32"; Relief Extension 75-160 Prefix=34"; Relief Height=72 1/8"; Relief NPT=3/4"; Relief Radius=3/8"; Shipping Weight lbs.=2780; Skid Length=102 1/8"; Skid Spacing=28"; Skid to Front=69 1/8"; Test Building Return Height=16 3/16"; Unit Height=88"; Unit Radius=28"; Vent Connection Housing Extension=8 3/8"; Vent Extension=31 3/8"; Vent Height=7 1/4"; Vent Location=4 11/16"
- 50 L 750A-TPX: 100 Prefix Recovery Rate 40F to 140F (gph)=-; 130 Prefix Recovery Rate 40F to 140F (gph)=-; 160 Prefix Recovery Rate 40F to 140F (gph)=-; 50 Prefix Recovery Rate 40F to 140F (gph)=587; 75 Prefix Recovery Rate 40F to 140F (gph)=-; Building Return Connection Height 50 (250-400gal only) prefix=1/2"; Building Return Connection Height 50-160 prefix=13 11/16"; Building Return Extension 250-400gal=1"; Building Return Extension 500-600gal=40 3/4"; Building Return Extension Angle 500-600gal=45.00°; Building Return Height=40"; Building Return Location=28 7/8"; Building Return NPT=1 1/2"; Building Return Radius=3/4"; Building Return to Economizer=14 1/16"; Burner Conn Height=76 1/8"; Burner Height=18 3/16"; Burner Housing -Y=15 5/8"; Burner Housing Extension=19"; Burner Housing to Left=5 3/16"; Burner Housing to Right=7 1/4"; Burner Nozzle Extension=12 3/8"; Cold Inlet Extension=38 3/8"; Cold Inlet NPT=3"; Cold Inlet Radius=1 1/2"; Combustion Air Connection X=15 7/16"; Combustion Air Connection to Right=3 9/16"; Condensate Extension=4 3/8"; Control Enclosure Angle=42.00°; Control Enclosure Location=41 5/16"; Control Panel Extension=40 1/2"; Drain Extension=35 1/8"; Drain NPT=1 1/2"; Drain Radius=3/4"; Economizer Connection Y=5 5/16"; Economizer Depth=10"; Economizer Inlet Outlet Connection Spacing=4"; Economizer Width=32"; Energy Height=33 11/16"; Flue Collector Extension=8 13/16"; Flue Collector Outlet to Front=3 11/16"; Flue Collector Radius=12 1/8"; Front Cowling Extension=41 1/4"; Gas Inlet NPT=1"; Gas Inlet Radius=1/2"; Gas Train Extension=17 3/8"; Gas Train To Front=10 11/16"; Gas Train Vertical=19 1/8"; Gas Train to Left=4 3/8"; Gas Train to Rear=10 1/8"; Height to Cold Inlet=21 5/16"; Height to Hot Outlet 400-1500gal=65 1/2"; Hot Outlet Angle=0.00°; Hot Outlet Extension=34 1/2"; Hot Outlet Radius=1 1/2"; Hot Outlet Side 400-1500gal NPT=0"; Hot Outlet Side Extension=34 1/2"; Hot Outlet Top 250-400gal NPT=3"; Input=500000 Btu/h; Model=50 L 750A-TPX; Pump Extension=37 7/8"; Pump Line Radius=5/8"; Pump Line to Economizer Location=36 1/8"; Rear Cowling Extension=1"; Relief Angle 50-160 Prefix=45.00°; Relief Angle 75-160 Prefix=38.00°; Relief Extension=37 1/2"; Relief Extension 50-160 Prefix=37 1/2"; Relief Extension 75-160 Prefix=10"; Relief Height=65 1/4"; Relief NPT=3/4"; Relief Radius=3/8"; Shipping Weight lbs.=2560; Skid Length=93 5/8"; Skid Spacing=37"; Skid to Front=55 1/8"; Test Building Return Height=20 11/16"; Unit Height=81 1/8"; Unit Radius=33 1/2"; Vent Connection Housing Extension=8 13/16"; Vent Extension=36 7/8"; Vent Height=6 7/8"; Vent Location=4"
- 75 L 750A-TPX: 100 Prefix Recovery Rate 40F to 140F (gph)=-; 130 Prefix Recovery Rate 40F to 140F (gph)=-; 160 Prefix Recovery Rate 40F to 140F (gph)=-; 50 Prefix Recovery Rate 40F to 140F (gph)=-; 75 Prefix Recovery Rate 40F to 140F (gph)=881; Building Return Connection Height 50 (250-400gal only) prefix=1/2"; Building Return Connection Height 50-160 prefix=13 11/16"; Building Return Extension 250-400gal=1"; Building Return Extension 500-600gal=40 3/4"; Building Return Extension Angle 500-600gal=45.00°; Building Return Height=40"; Building Return Location=28 7/8"; Building Return NPT=1 1/2"; Building Return Radius=3/4"; Building Return to Economizer=14 1/16"; Burner Conn Height=76 1/8"; Burner Height=18 3/16"; Burner Housing -Y=18 7/16"; Burner Housing Extension=20"; Burner Housing to Left=7 1/4"; Burner Housing to Right=7 7/8"; Burner Nozzle Extension=12 3/8"; Cold Inlet Extension=38 3/8"; Cold Inlet NPT=3"; Cold Inlet Radius=1 1/2"; Combustion Air Connection X=15 7/16"; Combustion Air Connection to Right=3 9/16"; Condensate Extension=4 3/8"; Control Enclosure Angle=42.00°; Control Enclosure Location=41 5/16"; Control Panel Extension=40 1/2"; Drain Extension=35 1/8"; Drain NPT=1 1/2"; Drain Radius=3/4"; Economizer Connection Y=5 5/16"; Economizer Depth=10"; Economizer Inlet Outlet Connection Spacing=4"; Economizer Width=32"; Energy Height=33 11/16"; Flue Collector Extension=8 13/16"; Flue Collector Outlet to Front=3 11/16"; Flue Collector Radius=12 1/8"; Front Cowling Extension=41 1/4"; Gas Inlet NPT=1"; Gas Inlet Radius=1/2"; Gas Train Extension=17 3/8"; Gas Train To Front=11 5/8"; Gas Train Vertical=19 1/8"; Gas Train to Left=4 3/8"; Gas Train to Rear=10 11/16"; Height to Cold Inlet=21 5/16"; Height to Hot Outlet 400-1500gal=65 1/2"; Hot Outlet Angle=0.00°; Hot Outlet Extension=34 1/2"; Hot Outlet Radius=1 1/2"; Hot Outlet Side 400-1500gal NPT=0"; Hot Outlet Side Extension=34 1/2"; Hot Outlet Top 250-400gal NPT=3"; Input=750000 Btu/h; Model=75 L 750A-TPX; Pump Extension=37 7/8"; Pump Line Radius=5/8"; Pump Line to Economizer Location=36 1/8"; Rear Cowling Extension=1"; Relief Angle 50-160 Prefix=45.00°; Relief Angle 75-160 Prefix=38.00°; Relief Extension=37 1/2"; Relief Extension 50-160 Prefix=37 1/2"; Relief Extension 75-160 Prefix=39 1/2"; Relief Height=65 1/4"; Relief NPT=3/4"; Relief Radius=3/8"; Shipping Weight lbs.=2640; Skid Length=93 5/8"; Skid Spacing=37"; Skid to Front=55 1/8"; Test Building Return Height=20 11/16"; Unit Height=81 1/8"; Unit Radius=33 1/2"; Vent Connection Housing Extension=8 13/16"; Vent Extension=36 7/8"; Vent Height=6 7/8"; Vent Location=4"
- 100 L 250A-TPX: 100 Prefix Recovery Rate 40F to 140F (gph)=1175; 130 Prefix Recovery Rate 40F to 140F (gph)=-; 160 Prefix Recovery Rate 40F to 140F (gph)=-; 50 Prefix Recovery Rate 40F to 140F (gph)=-; 75 Prefix Recovery Rate 40F to 140F (gph)=-; Building Return Connection Height 50 (250-400gal only) prefix=1/2"; Building Return Connection Height 50-160 prefix=14 3/16"; Building Return Extension 250-400gal=40 3/8"; Building Return Extension 500-600gal=5"; Building Return Extension Angle 500-600gal=45.00°; Building Return Height=18 3/16"; Building Return Location=28 1/2"; Building Return NPT=1 1/2"; Building Return Radius=3/4"; Building Return to Economizer=10 7/16"; Burner Conn Height=57 7/8"; Burner Height=18"; Burner Housing -Y=18 7/16"; Burner Housing Extension=20"; Burner Housing to Left=7 1/8"; Burner Housing to Right=7 7/8"; Burner Nozzle Extension=12 3/8"; Cold Inlet Extension=35 1/2"; Cold Inlet NPT=2"; Cold Inlet Radius=1"; Combustion Air Connection X=15 7/16"; Combustion Air Connection to Right=3 9/16"; Condensate Extension=4 3/8"; Control Enclosure Angle=56.00°; Control Enclosure Location=41 5/16"; Control Panel Extension=30"; Drain Extension=24 5/8"; Drain NPT=1"; Drain Radius=1/2"; Economizer Connection Y=5"; Economizer Depth=10"; Economizer Inlet Outlet Connection Spacing=4"; Economizer Width=32"; Energy Height=30 7/8"; Flue Collector Extension=8 13/16"; Flue Collector Outlet to Front=3 11/16"; Flue Collector Radius=12 1/8"; Front Cowling Extension=37 1/4"; Gas Inlet NPT=1"; Gas Inlet Radius=1/2"; Gas Train Extension=17 3/8"; Gas Train To Front=11 5/8"; Gas Train Vertical=20 5/8"; Gas Train to Left=4 3/8"; Gas Train to Rear=10 11/16"; Height to Cold Inlet=19 7/16"; Height to Hot Outlet 400-1500gal=45"; Hot Outlet Angle=90.00°; Hot Outlet Extension=24"; Hot Outlet Radius=1"; Hot Outlet Side 400-1500gal NPT=2"; Hot Outlet Side Extension=24"; Hot Outlet Top 250-400gal NPT=2"; Input=1000000 Btu/h; Model=100 L 250A-TPX; Pump Extension=27 3/8"; Pump Line Radius=5/8"; Pump Line to Economizer Location=31 11/16"; Rear Cowling Extension=1"; Relief Angle 50-160 Prefix=45.00°; Relief Angle 75-160 Prefix=30.00°; Relief Extension=27"; Relief Extension 50-160 Prefix=27"; Relief Extension 75-160 Prefix=29"; Relief Height=47"; Relief NPT=3/4"; Relief Radius=3/8"; Shipping Weight lbs.=2060; Skid Length=78 3/4"; Skid Spacing=28"; Skid to Front=51 1/16"; Test Building Return Height=16 3/16"; Unit Height=62 7/8"; Unit Radius=23"; Vent Connection Housing Extension=8 13/16"; Vent Extension=26 3/8"; Vent Height=7 1/4"; Vent Location=5 3/8"
- 100 L 300A-TPX: 100 Prefix Recovery Rate 40F to 140F (gph)=1175; 130 Prefix Recovery Rate 40F to 140F (gph)=-; 160 Prefix Recovery Rate 40F to 140F (gph)=-; 50 Prefix Recovery Rate 40F to 140F (gph)=-; 75 Prefix Recovery Rate 40F to 140F (gph)=-; Building Return Connection Height 50 (250-400gal only) prefix=1/2"; Building Return Connection Height 50-160 prefix=14 3/16"; Building Return Extension 250-400gal=40 3/8"; Building Return Extension 500-600gal=5"; Building Return Extension Angle 500-600gal=45.00°; Building Return Height=18 3/16"; Building Return Location=28 1/2"; Building Return NPT=1 1/2"; Building Return Radius=3/4"; Building Return to Economizer=10 7/16"; Burner Conn Height=69 7/8"; Burner Height=18"; Burner Housing -Y=18 7/16"; Burner Housing Extension=20"; Burner Housing to Left=7 1/8"; Burner Housing to Right=7 7/8"; Burner Nozzle Extension=12 3/8"; Cold Inlet Extension=35 1/2"; Cold Inlet NPT=2"; Cold Inlet Radius=1"; Combustion Air Connection X=15 7/16"; Combustion Air Connection to Right=3 9/16"; Condensate Extension=4 3/8"; Control Enclosure Angle=56.00°; Control Enclosure Location=51 1/4"; Control Panel Extension=30"; Drain Extension=24 5/8"; Drain NPT=1"; Drain Radius=1/2"; Economizer Connection Y=5"; Economizer Depth=10"; Economizer Inlet Outlet Connection Spacing=4"; Economizer Width=32"; Energy Height=30 7/8"; Flue Collector Extension=8 13/16"; Flue Collector Outlet to Front=3 11/16"; Flue Collector Radius=12 1/8"; Front Cowling Extension=37 1/4"; Gas Inlet NPT=1"; Gas Inlet Radius=1/2"; Gas Train Extension=17 3/8"; Gas Train To Front=11 5/8"; Gas Train Vertical=20 5/8"; Gas Train to Left=4 3/8"; Gas Train to Rear=10 11/16"; Height to Cold Inlet=19 7/16"; Height to Hot Outlet 400-1500gal=57"; Hot Outlet Angle=90.00°; Hot Outlet Extension=24"; Hot Outlet Radius=1"; Hot Outlet Side 400-1500gal NPT=0"; Hot Outlet Side Extension=1"; Hot Outlet Top 250-400gal NPT=2"; Input=1000000 Btu/h; Model=100 L 300A-TPX; Pump Extension=27 3/8"; Pump Line Radius=5/8"; Pump Line to Economizer Location=31 11/16"; Rear Cowling Extension=1"; Relief Angle 50-160 Prefix=45.00°; Relief Angle 75-160 Prefix=30.00°; Relief Extension=27"; Relief Extension 50-160 Prefix=27"; Relief Extension 75-160 Prefix=29"; Relief Height=59"; Relief NPT=3/4"; Relief Radius=3/8"; Shipping Weight lbs.=1890; Skid Length=78 3/4"; Skid Spacing=28"; Skid to Front=51 1/16"; Test Building Return Height=16 3/16"; Unit Height=74 7/8"; Unit Radius=23"; Vent Connection Housing Extension=8 13/16"; Vent Extension=26 3/8"; Vent Height=7 1/4"; Vent Location=5 3/8"
- 160 L 250A-TPX: 100 Prefix Recovery Rate 40F to 140F (gph)=-; 130 Prefix Recovery Rate 40F to 140F (gph)=-; 160 Prefix Recovery Rate 40F to 140F (gph)=1880; 50 Prefix Recovery Rate 40F to 140F (gph)=-; 75 Prefix Recovery Rate 40F to 140F (gph)=-; Building Return Connection Height 50 (250-400gal only) prefix=1/2"; Building Return Connection Height 50-160 prefix=14 1/2"; Building Return Extension 250-400gal=35 7/8"; Building Return Extension 500-600gal=5"; Building Return Extension Angle 500-600gal=45.00°; Building Return Height=18 3/16"; Building Return Location=25 3/8"; Building Return NPT=2"; Building Return Radius=1"; Building Return to Economizer=17"; Burner Conn Height=57 7/8"; Burner Height=18"; Burner Housing -Y=23 1/8"; Burner Housing Extension=24 1/4"; Burner Housing to Left=7 1/4"; Burner Housing to Right=11 1/2"; Burner Nozzle Extension=16 7/16"; Cold Inlet Extension=35 1/2"; Cold Inlet NPT=2"; Cold Inlet Radius=1"; Combustion Air Connection X=20"; Combustion Air Connection to Right=6 7/8"; Condensate Extension=4 3/8"; Control Enclosure Angle=56.00°; Control Enclosure Location=41 5/16"; Control Panel Extension=30"; Drain Extension=24 5/8"; Drain NPT=1"; Drain Radius=1/2"; Economizer Connection Y=5"; Economizer Depth=18"; Economizer Inlet Outlet Connection Spacing=7"; Economizer Width=32 3/4"; Energy Height=30 7/8"; Flue Collector Extension=13 1/8"; Flue Collector Outlet to Front=6 5/8"; Flue Collector Radius=12 1/8"; Front Cowling Extension=39 1/4"; Gas Inlet NPT=1 1/2"; Gas Inlet Radius=3/4"; Gas Train Extension=19 3/8"; Gas Train To Front=11 5/8"; Gas Train Vertical=24"; Gas Train to Left=6 5/8"; Gas Train to Rear=10 11/16"; Height to Cold Inlet=19 7/16"; Height to Hot Outlet 400-1500gal=45"; Hot Outlet Angle=90.00°; Hot Outlet Extension=24"; Hot Outlet Radius=1"; Hot Outlet Side 400-1500gal NPT=0"; Hot Outlet Side Extension=24"; Hot Outlet Top 250-400gal NPT=2"; Input=1600000 Btu/h; Model=160 L 250A-TPX; Pump Extension=27 3/8"; Pump Line Radius=1"; Pump Line to Economizer Location=31 11/16"; Rear Cowling Extension=43 5/16"; Relief Angle 50-160 Prefix=45.00°; Relief Angle 75-160 Prefix=30.00°; Relief Extension=27"; Relief Extension 50-160 Prefix=27"; Relief Extension 75-160 Prefix=29"; Relief Height=47"; Relief NPT=3/4"; Relief Radius=3/8"; Shipping Weight lbs.=2070; Skid Length=90 3/16"; Skid Spacing=28"; Skid to Front=60 7/8"; Test Building Return Height=16"; Unit Height=62 7/8"; Unit Radius=23"; Vent Connection Housing Extension=8 13/16"; Vent Extension=26 3/8"; Vent Height=7 1/4"; Vent Location=5 3/8"
- 160 L 300A-TPX: 100 Prefix Recovery Rate 40F to 140F (gph)=-; 130 Prefix Recovery Rate 40F to 140F (gph)=-; 160 Prefix Recovery Rate 40F to 140F (gph)=1880; 50 Prefix Recovery Rate 40F to 140F (gph)=-; 75 Prefix Recovery Rate 40F to 140F (gph)=-; Building Return Connection Height 50 (250-400gal only) prefix=1/2"; Building Return Connection Height 50-160 prefix=14 1/2"; Building Return Extension 250-400gal=35 7/8"; Building Return Extension 500-600gal=5"; Building Return Extension Angle 500-600gal=45.00°; Building Return Height=18 3/16"; Building Return Location=25 3/8"; Building Return NPT=2"; Building Return Radius=1"; Building Return to Economizer=17"; Burner Conn Height=69 7/8"; Burner Height=18"; Burner Housing -Y=23 1/8"; Burner Housing Extension=24 1/4"; Burner Housing to Left=7 1/4"; Burner Housing to Right=11 1/2"; Burner Nozzle Extension=16 7/16"; Cold Inlet Extension=35 1/2"; Cold Inlet NPT=2"; Cold Inlet Radius=1"; Combustion Air Connection X=20"; Combustion Air Connection to Right=6 7/8"; Condensate Extension=4 3/8"; Control Enclosure Angle=56.00°; Control Enclosure Location=51 1/4"; Control Panel Extension=30"; Drain Extension=24 5/8"; Drain NPT=1"; Drain Radius=1/2"; Economizer Connection Y=5"; Economizer Depth=18"; Economizer Inlet Outlet Connection Spacing=7"; Economizer Width=32 3/4"; Energy Height=30 7/8"; Flue Collector Extension=13 1/8"; Flue Collector Outlet to Front=6 5/8"; Flue Collector Radius=12 1/8"; Front Cowling Extension=39 1/4"; Gas Inlet NPT=1 1/2"; Gas Inlet Radius=3/4"; Gas Train Extension=19 3/8"; Gas Train To Front=11 5/8"; Gas Train Vertical=24"; Gas Train to Left=6 5/8"; Gas Train to Rear=10 11/16"; Height to Cold Inlet=19 7/16"; Height to Hot Outlet 400-1500gal=57"; Hot Outlet Angle=90.00°; Hot Outlet Extension=24"; Hot Outlet Radius=1"; Hot Outlet Side 400-1500gal NPT=0"; Hot Outlet Side Extension=24"; Hot Outlet Top 250-400gal NPT=2"; Input=1600000 Btu/h; Model=160 L 300A-TPX; Pump Extension=27 3/8"; Pump Line Radius=1"; Pump Line to Economizer Location=31 11/16"; Rear Cowling Extension=43 5/16"; Relief Angle 50-160 Prefix=45.00°; Relief Angle 75-160 Prefix=30.00°; Relief Extension=27"; Relief Extension 50-160 Prefix=27"; Relief Extension 75-160 Prefix=29"; Relief Height=59"; Relief NPT=3/4"; Relief Radius=3/8"; Shipping Weight lbs.=2130; Skid Length=90 3/16"; Skid Spacing=28"; Skid to Front=60 7/8"; Test Building Return Height=16 3/16"; Unit Height=74 7/8"; Unit Radius=23"; Vent Connection Housing Extension=8 13/16"; Vent Extension=26 3/8"; Vent Height=7 1/4"; Vent Location=5 3/8"
- 100 L 400A-TPX: 100 Prefix Recovery Rate 40F to 140F (gph)=1175; 130 Prefix Recovery Rate 40F to 140F (gph)=-; 160 Prefix Recovery Rate 40F to 140F (gph)=-; 50 Prefix Recovery Rate 40F to 140F (gph)=-; 75 Prefix Recovery Rate 40F to 140F (gph)=-; Building Return Connection Height 50 (250-400gal only) prefix=1/2"; Building Return Connection Height 50-160 prefix=14 3/16"; Building Return Extension 250-400gal=40 3/8"; Building Return Extension 500-600gal=5"; Building Return Extension Angle 500-600gal=45.00°; Building Return Height=18 3/16"; Building Return Location=28 1/2"; Building Return NPT=1 1/2"; Building Return Radius=3/4"; Building Return to Economizer=10 7/16"; Burner Conn Height=81 7/8"; Burner Height=18"; Burner Housing -Y=18 7/16"; Burner Housing Extension=20"; Burner Housing to Left=7 1/8"; Burner Housing to Right=7 7/8"; Burner Nozzle Extension=12 3/8"; Cold Inlet Extension=35 1/2"; Cold Inlet NPT=2"; Cold Inlet Radius=1"; Combustion Air Connection X=15 7/16"; Combustion Air Connection to Right=3 9/16"; Condensate Extension=4 3/8"; Control Enclosure Angle=56.00°; Control Enclosure Location=51 1/4"; Control Panel Extension=30"; Drain Extension=24 5/8"; Drain NPT=1"; Drain Radius=1/2"; Economizer Connection Y=5"; Economizer Depth=10"; Economizer Inlet Outlet Connection Spacing=4"; Economizer Width=32"; Energy Height=30 7/8"; Flue Collector Extension=8 13/16"; Flue Collector Outlet to Front=3 11/16"; Flue Collector Radius=12 1/8"; Front Cowling Extension=37 1/4"; Gas Inlet NPT=1"; Gas Inlet Radius=1/2"; Gas Train Extension=17 3/8"; Gas Train To Front=11 5/8"; Gas Train Vertical=20 5/8"; Gas Train to Left=4 3/8"; Gas Train to Rear=10 11/16"; Height to Cold Inlet=19 7/16"; Height to Hot Outlet 400-1500gal=73 1/2"; Hot Outlet Angle=0.00°; Hot Outlet Extension=24"; Hot Outlet Radius=1"; Hot Outlet Side 400-1500gal NPT=0"; Hot Outlet Side Extension=24"; Hot Outlet Top 250-400gal NPT=2"; Input=1000000 Btu/h; Model=100 L 400A-TPX; Pump Extension=27 3/8"; Pump Line Radius=5/8"; Pump Line to Economizer Location=31 11/16"; Rear Cowling Extension=1"; Relief Angle 50-160 Prefix=45.00°; Relief Angle 75-160 Prefix=30.00°; Relief Extension=27"; Relief Extension 50-160 Prefix=27"; Relief Extension 75-160 Prefix=29"; Relief Height=71"; Relief NPT=1"; Relief Radius=1/2"; Shipping Weight lbs.=1885; Skid Length=78 3/4"; Skid Spacing=28"; Skid to Front=51 1/16"; Test Building Return Height=16 3/16"; Unit Height=86 7/8"; Unit Radius=23"; Vent Connection Housing Extension=8 13/16"; Vent Extension=26 3/8"; Vent Height=7 1/4"; Vent Location=5 3/8"
- 160 L 400A-TPX: 100 Prefix Recovery Rate 40F to 140F (gph)=-; 130 Prefix Recovery Rate 40F to 140F (gph)=-; 160 Prefix Recovery Rate 40F to 140F (gph)=1880; 50 Prefix Recovery Rate 40F to 140F (gph)=-; 75 Prefix Recovery Rate 40F to 140F (gph)=-; Building Return Connection Height 50 (250-400gal only) prefix=1/2"; Building Return Connection Height 50-160 prefix=14 1/2"; Building Return Extension 250-400gal=35 7/8"; Building Return Extension 500-600gal=5"; Building Return Extension Angle 500-600gal=45.00°; Building Return Height=18 3/16"; Building Return Location=25 3/8"; Building Return NPT=2"; Building Return Radius=1"; Building Return to Economizer=17"; Burner Conn Height=81 7/8"; Burner Height=18"; Burner Housing -Y=23 1/8"; Burner Housing Extension=24 1/4"; Burner Housing to Left=7 1/4"; Burner Housing to Right=11 1/2"; Burner Nozzle Extension=16 7/16"; Cold Inlet Extension=35 1/2"; Cold Inlet NPT=2"; Cold Inlet Radius=1"; Combustion Air Connection X=20"; Combustion Air Connection to Right=6 7/8"; Condensate Extension=4 3/8"; Control Enclosure Angle=56.00°; Control Enclosure Location=51 1/4"; Control Panel Extension=30"; Drain Extension=24 5/8"; Drain NPT=1"; Drain Radius=1/2"; Economizer Connection Y=5"; Economizer Depth=18"; Economizer Inlet Outlet Connection Spacing=7"; Economizer Width=32 3/4"; Energy Height=30 7/8"; Flue Collector Extension=13 1/8"; Flue Collector Outlet to Front=6 5/8"; Flue Collector Radius=12 1/8"; Front Cowling Extension=39 1/4"; Gas Inlet NPT=1 1/2"; Gas Inlet Radius=3/4"; Gas Train Extension=19 3/8"; Gas Train To Front=11 5/8"; Gas Train Vertical=24"; Gas Train to Left=6 5/8"; Gas Train to Rear=10 11/16"; Height to Cold Inlet=19 7/16"; Height to Hot Outlet 400-1500gal=73 1/2"; Hot Outlet Angle=0.00°; Hot Outlet Extension=24"; Hot Outlet Radius=1"; Hot Outlet Side 400-1500gal NPT=0"; Hot Outlet Side Extension=24"; Hot Outlet Top 250-400gal NPT=2"; Input=1600000 Btu/h; Model=160 L 400A-TPX; Pump Extension=27 3/8"; Pump Line Radius=1"; Pump Line to Economizer Location=31 11/16"; Rear Cowling Extension=43 5/16"; Relief Angle 50-160 Prefix=45.00°; Relief Angle 75-160 Prefix=30.00°; Relief Extension=27"; Relief Extension 50-160 Prefix=27"; Relief Extension 75-160 Prefix=29"; Relief Height=71"; Relief NPT=3/4"; Relief Radius=3/8"; Shipping Weight lbs.=2165; Skid Length=90 3/16"; Skid Spacing=28"; Skid to Front=60 7/8"; Test Building Return Height=16 3/16"; Unit Height=86 7/8"; Unit Radius=23"; Vent Connection Housing Extension=8 13/16"; Vent Extension=26 3/8"; Vent Height=7 1/4"; Vent Location=5 3/8"
- 100 L 500A-TPX: 100 Prefix Recovery Rate 40F to 140F (gph)=1175; 130 Prefix Recovery Rate 40F to 140F (gph)=-; 160 Prefix Recovery Rate 40F to 140F (gph)=-; 50 Prefix Recovery Rate 40F to 140F (gph)=-; 75 Prefix Recovery Rate 40F to 140F (gph)=-; Building Return Connection Height 50 (250-400gal only) prefix=1/2"; Building Return Connection Height 50-160 prefix=14 3/8"; Building Return Extension 250-400gal=1"; Building Return Extension 500-600gal=35 25/32"; Building Return Extension Angle 500-600gal=35.00°; Building Return Height=18 3/8"; Building Return Location=29 3/16"; Building Return NPT=1 1/2"; Building Return Radius=3/4"; Building Return to Economizer=17 9/16"; Burner Conn Height=71"; Burner Height=18"; Burner Housing -Y=18 7/16"; Burner Housing Extension=20"; Burner Housing to Left=7 1/8"; Burner Housing to Right=7 7/8"; Burner Nozzle Extension=12 3/8"; Cold Inlet Extension=34 3/4"; Cold Inlet NPT=3"; Cold Inlet Radius=1 1/2"; Combustion Air Connection X=15 7/16"; Combustion Air Connection to Right=3 9/16"; Condensate Extension=4 3/8"; Control Enclosure Angle=45.00°; Control Enclosure Location=41 5/16"; Control Panel Extension=35"; Drain Extension=29 5/8"; Drain NPT=1 1/2"; Drain Radius=3/4"; Economizer Connection Y=5"; Economizer Depth=10"; Economizer Inlet Outlet Connection Spacing=4"; Economizer Width=32"; Energy Height=30 7/8"; Flue Collector Extension=8 13/16"; Flue Collector Outlet to Front=3 11/16"; Flue Collector Radius=12 1/8"; Front Cowling Extension=36 1/4"; Gas Inlet NPT=1"; Gas Inlet Radius=1/2"; Gas Train Extension=17 3/8"; Gas Train To Front=10 11/16"; Gas Train Vertical=20 5/8"; Gas Train to Left=4 3/8"; Gas Train to Rear=9 11/16"; Height to Cold Inlet=19 7/16"; Height to Hot Outlet 400-1500gal=62 1/2"; Hot Outlet Angle=0.00°; Hot Outlet Extension=29"; Hot Outlet Radius=1 1/2"; Hot Outlet Side 400-1500gal NPT=0"; Hot Outlet Side Extension=29"; Hot Outlet Top 250-400gal NPT=3"; Input=1000000 Btu/h; Model=100 L 500A-TPX; Pump Extension=32 3/8"; Pump Line Radius=5/8"; Pump Line to Economizer Location=32 1/2"; Rear Cowling Extension=1"; Relief Angle 50-160 Prefix=35.00°; Relief Angle 75-160 Prefix=27.00°; Relief Extension=32"; Relief Extension 50-160 Prefix=32"; Relief Extension 75-160 Prefix=34"; Relief Height=60 1/8"; Relief NPT=3/4"; Relief Radius=3/8"; Shipping Weight lbs.=2315; Skid Length=82 7/8"; Skid Spacing=28"; Skid to Front=49 7/8"; Test Building Return Height=16 3/16"; Unit Height=76"; Unit Radius=28"; Vent Connection Housing Extension=8 13/16"; Vent Extension=31 3/8"; Vent Height=7 1/4"; Vent Location=5 3/8"
- 160 L 500A-TPX: 100 Prefix Recovery Rate 40F to 140F (gph)=-; 130 Prefix Recovery Rate 40F to 140F (gph)=-; 160 Prefix Recovery Rate 40F to 140F (gph)=1880; 50 Prefix Recovery Rate 40F to 140F (gph)=-; 75 Prefix Recovery Rate 40F to 140F (gph)=-; Building Return Connection Height 50 (250-400gal only) prefix=1/2"; Building Return Connection Height 50-160 prefix=14 3/8"; Building Return Extension 250-400gal=1"; Building Return Extension 500-600gal=35 25/32"; Building Return Extension Angle 500-600gal=34.75°; Building Return Height=18 3/8"; Building Return Location=29 3/16"; Building Return NPT=2"; Building Return Radius=1"; Building Return to Economizer=31"; Burner Conn Height=71"; Burner Height=18"; Burner Housing -Y=19 7/16"; Burner Housing Extension=24 1/4"; Burner Housing to Left=7 1/4"; Burner Housing to Right=11 1/2"; Burner Nozzle Extension=16 7/16"; Cold Inlet Extension=35 1/4"; Cold Inlet NPT=3"; Cold Inlet Radius=1 1/2"; Combustion Air Connection X=20"; Combustion Air Connection to Right=6 7/8"; Condensate Extension=4 3/16"; Control Enclosure Angle=45.00°; Control Enclosure Location=41 5/16"; Control Panel Extension=35"; Drain Extension=29 5/8"; Drain NPT=1 1/2"; Drain Radius=3/4"; Economizer Connection Y=5"; Economizer Depth=18"; Economizer Inlet Outlet Connection Spacing=7"; Economizer Width=32 3/4"; Energy Height=30 7/8"; Flue Collector Extension=13 1/8"; Flue Collector Outlet to Front=6 5/8"; Flue Collector Radius=11 13/16"; Front Cowling Extension=48 3/16"; Gas Inlet NPT=1"; Gas Inlet Radius=1/2"; Gas Train Extension=19 3/8"; Gas Train To Front=11 5/8"; Gas Train Vertical=24"; Gas Train to Left=6 5/8"; Gas Train to Rear=10 11/16"; Height to Cold Inlet=19 1/8"; Height to Hot Outlet 400-1500gal=62 1/2"; Hot Outlet Angle=0.00°; Hot Outlet Extension=29"; Hot Outlet Radius=1 1/2"; Hot Outlet Side 400-1500gal NPT=0"; Hot Outlet Side Extension=29"; Hot Outlet Top 250-400gal NPT=3"; Input=1600000 Btu/h; Model=160 L 500A-TPX; Pump Extension=32 3/8"; Pump Line Radius=1"; Pump Line to Economizer Location=32 13/16"; Rear Cowling Extension=33 5/8"; Relief Angle 50-160 Prefix=35.00°; Relief Angle 75-160 Prefix=27.00°; Relief Extension=32"; Relief Extension 50-160 Prefix=32"; Relief Extension 75-160 Prefix=34"; Relief Height=60 1/8"; Relief NPT=3/4"; Relief Radius=3/8"; Shipping Weight lbs.=2555; Skid Length=102 1/8"; Skid Spacing=28"; Skid to Front=69 1/8"; Test Building Return Height=16 3/16"; Unit Height=76"; Unit Radius=28"; Vent Connection Housing Extension=8 3/8"; Vent Extension=31 3/8"; Vent Height=7 1/4"; Vent Location=4 11/16"
- 100 L 600A-TPX: 100 Prefix Recovery Rate 40F to 140F (gph)=1175; 130 Prefix Recovery Rate 40F to 140F (gph)=-; 160 Prefix Recovery Rate 40F to 140F (gph)=-; 50 Prefix Recovery Rate 40F to 140F (gph)=-; 75 Prefix Recovery Rate 40F to 140F (gph)=-; Building Return Connection Height 50 (250-400gal only) prefix=1/2"; Building Return Connection Height 50-160 prefix=14 3/8"; Building Return Extension 250-400gal=1"; Building Return Extension 500-600gal=35 25/32"; Building Return Extension Angle 500-600gal=35.00°; Building Return Height=18 3/8"; Building Return Location=29 3/16"; Building Return NPT=1 1/2"; Building Return Radius=3/4"; Building Return to Economizer=17 9/16"; Burner Conn Height=83 5/8"; Burner Height=18"; Burner Housing -Y=18 7/16"; Burner Housing Extension=20"; Burner Housing to Left=7 1/8"; Burner Housing to Right=7 7/8"; Burner Nozzle Extension=12 3/8"; Cold Inlet Extension=34 3/4"; Cold Inlet NPT=3"; Cold Inlet Radius=1 1/2"; Combustion Air Connection X=15 7/16"; Combustion Air Connection to Right=3 9/16"; Condensate Extension=4 3/8"; Control Enclosure Angle=45.00°; Control Enclosure Location=41 5/16"; Control Panel Extension=35"; Drain Extension=29 5/8"; Drain NPT=1 1/2"; Drain Radius=3/4"; Economizer Connection Y=5"; Economizer Depth=10"; Economizer Inlet Outlet Connection Spacing=4"; Economizer Width=32"; Energy Height=30 7/8"; Flue Collector Extension=8 13/16"; Flue Collector Outlet to Front=3 11/16"; Flue Collector Radius=12 1/8"; Front Cowling Extension=36 1/4"; Gas Inlet NPT=1"; Gas Inlet Radius=1/2"; Gas Train Extension=17 3/8"; Gas Train To Front=10 11/16"; Gas Train Vertical=20 5/8"; Gas Train to Left=4 3/8"; Gas Train to Rear=9 11/16"; Height to Cold Inlet=19 7/16"; Height to Hot Outlet 400-1500gal=74 1/2"; Hot Outlet Angle=0.00°; Hot Outlet Extension=29"; Hot Outlet Radius=1 1/2"; Hot Outlet Side 400-1500gal NPT=0"; Hot Outlet Side Extension=29"; Hot Outlet Top 250-400gal NPT=3"; Input=1000000 Btu/h; Model=100 L 600A-TPX; Pump Extension=32 3/8"; Pump Line Radius=5/8"; Pump Line to Economizer Location=32 1/2"; Rear Cowling Extension=1"; Relief Angle 50-160 Prefix=35.00°; Relief Angle 75-160 Prefix=27.00°; Relief Extension=32"; Relief Extension 50-160 Prefix=32"; Relief Extension 75-160 Prefix=34"; Relief Height=72 3/4"; Relief NPT=3/4"; Relief Radius=3/8"; Shipping Weight lbs.=2550; Skid Length=82 7/8"; Skid Spacing=28"; Skid to Front=49 7/8"; Test Building Return Height=16 3/16"; Unit Height=88 5/8"; Unit Radius=28"; Vent Connection Housing Extension=8 13/16"; Vent Extension=31 3/8"; Vent Height=7 1/4"; Vent Location=5 3/8"
- 160 L 600A-TPX: 100 Prefix Recovery Rate 40F to 140F (gph)=-; 130 Prefix Recovery Rate 40F to 140F (gph)=-; 160 Prefix Recovery Rate 40F to 140F (gph)=1880; 50 Prefix Recovery Rate 40F to 140F (gph)=-; 75 Prefix Recovery Rate 40F to 140F (gph)=-; Building Return Connection Height 50 (250-400gal only) prefix=1/2"; Building Return Connection Height 50-160 prefix=14 3/8"; Building Return Extension 250-400gal=1"; Building Return Extension 500-600gal=35 25/32"; Building Return Extension Angle 500-600gal=34.75°; Building Return Height=18 3/8"; Building Return Location=29 3/16"; Building Return NPT=2"; Building Return Radius=1"; Building Return to Economizer=31"; Burner Conn Height=83"; Burner Height=18"; Burner Housing -Y=19 7/16"; Burner Housing Extension=24 1/4"; Burner Housing to Left=7 1/4"; Burner Housing to Right=11 1/2"; Burner Nozzle Extension=16 7/16"; Cold Inlet Extension=35 1/4"; Cold Inlet NPT=3"; Cold Inlet Radius=1 1/2"; Combustion Air Connection X=20"; Combustion Air Connection to Right=6 7/8"; Condensate Extension=4 3/16"; Control Enclosure Angle=45.00°; Control Enclosure Location=41 5/16"; Control Panel Extension=35"; Drain Extension=29 5/8"; Drain NPT=1 1/2"; Drain Radius=3/4"; Economizer Connection Y=5"; Economizer Depth=18"; Economizer Inlet Outlet Connection Spacing=7"; Economizer Width=32 3/4"; Energy Height=30 7/8"; Flue Collector Extension=13 1/8"; Flue Collector Outlet to Front=6 5/8"; Flue Collector Radius=11 13/16"; Front Cowling Extension=48 3/16"; Gas Inlet NPT=1"; Gas Inlet Radius=1/2"; Gas Train Extension=19 3/8"; Gas Train To Front=11 5/8"; Gas Train Vertical=24"; Gas Train to Left=6 5/8"; Gas Train to Rear=10 11/16"; Height to Cold Inlet=19 1/8"; Height to Hot Outlet 400-1500gal=74 1/2"; Hot Outlet Angle=0.00°; Hot Outlet Extension=29"; Hot Outlet Radius=1 1/2"; Hot Outlet Side 400-1500gal NPT=0"; Hot Outlet Side Extension=29"; Hot Outlet Top 250-400gal NPT=3"; Input=1600000 Btu/h; Model=160 L 600A-TPX; Pump Extension=32 3/8"; Pump Line Radius=1"; Pump Line to Economizer Location=32 13/16"; Rear Cowling Extension=33 5/8"; Relief Angle 50-160 Prefix=35.00°; Relief Angle 75-160 Prefix=27.00°; Relief Extension=32"; Relief Extension 50-160 Prefix=32"; Relief Extension 75-160 Prefix=34"; Relief Height=72 1/8"; Relief NPT=3/4"; Relief Radius=3/8"; Shipping Weight lbs.=2790; Skid Length=102 1/8"; Skid Spacing=28"; Skid to Front=69 1/8"; Test Building Return Height=16 3/16"; Unit Height=88"; Unit Radius=28"; Vent Connection Housing Extension=8 3/8"; Vent Extension=31 3/8"; Vent Height=7 1/4"; Vent Location=4 11/16"
- 100 L 750A-TPX: 100 Prefix Recovery Rate 40F to 140F (gph)=1175; 130 Prefix Recovery Rate 40F to 140F (gph)=-; 160 Prefix Recovery Rate 40F to 140F (gph)=-; 50 Prefix Recovery Rate 40F to 140F (gph)=-; 75 Prefix Recovery Rate 40F to 140F (gph)=-; Building Return Connection Height 50 (250-400gal only) prefix=1/2"; Building Return Connection Height 50-160 prefix=13 11/16"; Building Return Extension 250-400gal=1"; Building Return Extension 500-600gal=40 3/4"; Building Return Extension Angle 500-600gal=45.00°; Building Return Height=40"; Building Return Location=28 7/8"; Building Return NPT=1 1/2"; Building Return Radius=3/4"; Building Return to Economizer=14 1/16"; Burner Conn Height=76 1/8"; Burner Height=18 3/16"; Burner Housing -Y=18 7/16"; Burner Housing Extension=20"; Burner Housing to Left=7 1/4"; Burner Housing to Right=7 7/8"; Burner Nozzle Extension=12 3/8"; Cold Inlet Extension=38 3/8"; Cold Inlet NPT=3"; Cold Inlet Radius=1 1/2"; Combustion Air Connection X=15 7/16"; Combustion Air Connection to Right=3 9/16"; Condensate Extension=4 3/8"; Control Enclosure Angle=55.00°; Control Enclosure Location=41 5/16"; Control Panel Extension=40 1/2"; Drain Extension=35 1/8"; Drain NPT=1 1/2"; Drain Radius=3/4"; Economizer Connection Y=5 5/16"; Economizer Depth=10"; Economizer Inlet Outlet Connection Spacing=4"; Economizer Width=32"; Energy Height=33 11/16"; Flue Collector Extension=8 13/16"; Flue Collector Outlet to Front=3 11/16"; Flue Collector Radius=12 1/8"; Front Cowling Extension=41 1/4"; Gas Inlet NPT=1"; Gas Inlet Radius=1/2"; Gas Train Extension=17 3/8"; Gas Train To Front=11 5/8"; Gas Train Vertical=19 1/8"; Gas Train to Left=4 3/8"; Gas Train to Rear=10 11/16"; Height to Cold Inlet=21 5/16"; Height to Hot Outlet 400-1500gal=67"; Hot Outlet Angle=0.00°; Hot Outlet Extension=34 1/2"; Hot Outlet Radius=1 1/2"; Hot Outlet Side 400-1500gal NPT=0"; Hot Outlet Side Extension=34 1/2"; Hot Outlet Top 250-400gal NPT=3"; Input=1000000 Btu/h; Model=100 L 750A-TPX; Pump Extension=37 7/8"; Pump Line Radius=5/8"; Pump Line to Economizer Location=36 1/8"; Rear Cowling Extension=1"; Relief Angle 50-160 Prefix=45.00°; Relief Angle 75-160 Prefix=38.00°; Relief Extension=37 1/2"; Relief Extension 50-160 Prefix=37 1/2"; Relief Extension 75-160 Prefix=39 1/2"; Relief Height=65 1/4"; Relief NPT=3/4"; Relief Radius=3/8"; Shipping Weight lbs.=2680; Skid Length=93 5/8"; Skid Spacing=37"; Skid to Front=55 1/8"; Test Building Return Height=20 11/16"; Unit Height=81 1/8"; Unit Radius=33 1/2"; Vent Connection Housing Extension=8 13/16"; Vent Extension=36 7/8"; Vent Height=6 7/8"; Vent Location=4"
- 130 L 750A-TPX: 100 Prefix Recovery Rate 40F to 140F (gph)=-; 130 Prefix Recovery Rate 40F to 140F (gph)=1527; 160 Prefix Recovery Rate 40F to 140F (gph)=-; 50 Prefix Recovery Rate 40F to 140F (gph)=-; 75 Prefix Recovery Rate 40F to 140F (gph)=-; Building Return Connection Height 50 (250-400gal only) prefix=1/2"; Building Return Connection Height 50-160 prefix=14 3/8"; Building Return Extension 250-400gal=1"; Building Return Extension 500-600gal=40 7/8"; Building Return Extension Angle 500-600gal=45.00°; Building Return Height=40"; Building Return Location=28 7/8"; Building Return NPT=2"; Building Return Radius=1"; Building Return to Economizer=27 7/8"; Burner Conn Height=76 1/8"; Burner Height=18"; Burner Housing -Y=19 7/16"; Burner Housing Extension=24 1/4"; Burner Housing to Left=7 1/4"; Burner Housing to Right=11 1/2"; Burner Nozzle Extension=16 3/4"; Cold Inlet Extension=38 7/8"; Cold Inlet NPT=3"; Cold Inlet Radius=1 1/2"; Combustion Air Connection X=15 7/16"; Combustion Air Connection to Right=3 9/16"; Condensate Extension=4 3/16"; Control Enclosure Angle=42.00°; Control Enclosure Location=41 5/16"; Control Panel Extension=40 1/2"; Drain Extension=35 1/8"; Drain NPT=1 1/2"; Drain Radius=3/4"; Economizer Connection Y=5"; Economizer Depth=18"; Economizer Inlet Outlet Connection Spacing=7"; Economizer Width=32 3/4"; Energy Height=33 11/16"; Flue Collector Extension=13 1/4"; Flue Collector Outlet to Front=6 5/8"; Flue Collector Radius=11 13/16"; Front Cowling Extension=53 5/8"; Gas Inlet NPT=1"; Gas Inlet Radius=1/2"; Gas Train Extension=19 3/8"; Gas Train To Front=11 5/8"; Gas Train Vertical=24"; Gas Train to Left=6 5/8"; Gas Train to Rear=10 11/16"; Height to Cold Inlet=21 5/16"; Height to Hot Outlet 400-1500gal=65 1/2"; Hot Outlet Angle=0.00°; Hot Outlet Extension=34 1/2"; Hot Outlet Radius=1 1/2"; Hot Outlet Side 400-1500gal NPT=0"; Hot Outlet Side Extension=34 1/2"; Hot Outlet Top 250-400gal NPT=3"; Input=1300000 Btu/h; Model=130 L 750A-TPX; Pump Extension=37 7/8"; Pump Line Radius=1"; Pump Line to Economizer Location=36 5/16"; Rear Cowling Extension=1"; Relief Angle 50-160 Prefix=45.00°; Relief Angle 75-160 Prefix=38.00°; Relief Extension=37 1/2"; Relief Extension 50-160 Prefix=37 1/2"; Relief Extension 75-160 Prefix=39 1/2"; Relief Height=65 1/4"; Relief NPT=3/4"; Relief Radius=3/8"; Shipping Weight lbs.=2910; Skid Length=113"; Skid Spacing=37"; Skid to Front=74 3/4"; Test Building Return Height=20 11/16"; Unit Height=81 1/8"; Unit Radius=33 1/2"; Vent Connection Housing Extension=8 13/16"; Vent Extension=36 7/8"; Vent Height=7 1/4"; Vent Location=4 11/16"
- 160 L 750A-TPX: 100 Prefix Recovery Rate 40F to 140F (gph)=-; 130 Prefix Recovery Rate 40F to 140F (gph)=-; 160 Prefix Recovery Rate 40F to 140F (gph)=1880; 50 Prefix Recovery Rate 40F to 140F (gph)=-; 75 Prefix Recovery Rate 40F to 140F (gph)=-; Building Return Connection Height 50 (250-400gal only) prefix=1/2"; Building Return Connection Height 50-160 prefix=14 3/8"; Building Return Extension 250-400gal=1"; Building Return Extension 500-600gal=40 7/8"; Building Return Extension Angle 500-600gal=45.00°; Building Return Height=40"; Building Return Location=28 7/8"; Building Return NPT=2"; Building Return Radius=1"; Building Return to Economizer=27 7/8"; Burner Conn Height=76 1/8"; Burner Height=18"; Burner Housing -Y=19 7/16"; Burner Housing Extension=24 1/4"; Burner Housing to Left=7 1/4"; Burner Housing to Right=11 1/2"; Burner Nozzle Extension=16 3/4"; Cold Inlet Extension=38 7/8"; Cold Inlet NPT=3"; Cold Inlet Radius=1 1/2"; Combustion Air Connection X=15 7/16"; Combustion Air Connection to Right=3 9/16"; Condensate Extension=4 3/16"; Control Enclosure Angle=42.00°; Control Enclosure Location=41 5/16"; Control Panel Extension=40 1/2"; Drain Extension=35 1/8"; Drain NPT=1 1/2"; Drain Radius=3/4"; Economizer Connection Y=5"; Economizer Depth=18"; Economizer Inlet Outlet Connection Spacing=7"; Economizer Width=32 3/4"; Energy Height=33 11/16"; Flue Collector Extension=13 1/4"; Flue Collector Outlet to Front=6 5/8"; Flue Collector Radius=12 1/8"; Front Cowling Extension=53 5/8"; Gas Inlet NPT=1"; Gas Inlet Radius=1/2"; Gas Train Extension=19 3/8"; Gas Train To Front=11 5/8"; Gas Train Vertical=24"; Gas Train to Left=6 5/8"; Gas Train to Rear=10 11/16"; Height to Cold Inlet=21 5/16"; Height to Hot Outlet 400-1500gal=65 1/2"; Hot Outlet Angle=0.00°; Hot Outlet Extension=34 1/2"; Hot Outlet Radius=1 1/2"; Hot Outlet Side 400-1500gal NPT=0"; Hot Outlet Side Extension=34 1/2"; Hot Outlet Top 250-400gal NPT=3"; Input=1600000 Btu/h; Model=160 L 750A-TPX; Pump Extension=37 7/8"; Pump Line Radius=1"; Pump Line to Economizer Location=36 5/16"; Rear Cowling Extension=1"; Relief Angle 50-160 Prefix=45.00°; Relief Angle 75-160 Prefix=38.00°; Relief Extension=37 1/2"; Relief Extension 50-160 Prefix=37 1/2"; Relief Extension 75-160 Prefix=39 1/2"; Relief Height=65 1/4"; Relief NPT=3/4"; Relief Radius=3/8"; Shipping Weight lbs.=2920; Skid Length=113"; Skid Spacing=37"; Skid to Front=74 3/4"; Test Building Return Height=20 11/16"; Unit Height=81 1/8"; Unit Radius=33 1/2"; Vent Connection Housing Extension=8 13/16"; Vent Extension=36 7/8"; Vent Height=7 1/4"; Vent Location=4 11/16"
- 50 L 900A-TPX: 100 Prefix Recovery Rate 40F to 140F (gph)=-; 130 Prefix Recovery Rate 40F to 140F (gph)=-; 160 Prefix Recovery Rate 40F to 140F (gph)=-; 50 Prefix Recovery Rate 40F to 140F (gph)=587; 75 Prefix Recovery Rate 40F to 140F (gph)=-; Building Return Connection Height 50 (250-400gal only) prefix=1/2"; Building Return Connection Height 50-160 prefix=13 11/16"; Building Return Extension 250-400gal=1"; Building Return Extension 500-600gal=40 3/4"; Building Return Extension Angle 500-600gal=45.00°; Building Return Height=40"; Building Return Location=28 7/8"; Building Return NPT=1 1/2"; Building Return Radius=3/4"; Building Return to Economizer=14 1/16"; Burner Conn Height=88 9/16"; Burner Height=18 3/16"; Burner Housing -Y=15 5/8"; Burner Housing Extension=19"; Burner Housing to Left=5 3/16"; Burner Housing to Right=7 1/4"; Burner Nozzle Extension=12 3/8"; Cold Inlet Extension=38 3/8"; Cold Inlet NPT=3"; Cold Inlet Radius=1 1/2"; Combustion Air Connection X=15 7/16"; Combustion Air Connection to Right=3 9/16"; Condensate Extension=4 3/8"; Control Enclosure Angle=42.00°; Control Enclosure Location=41 5/16"; Control Panel Extension=40 1/2"; Drain Extension=35 1/8"; Drain NPT=1 1/2"; Drain Radius=3/4"; Economizer Connection Y=5 5/16"; Economizer Depth=10"; Economizer Inlet Outlet Connection Spacing=4"; Economizer Width=32"; Energy Height=33 11/16"; Flue Collector Extension=8 13/16"; Flue Collector Outlet to Front=3 11/16"; Flue Collector Radius=12 1/8"; Front Cowling Extension=41 1/4"; Gas Inlet NPT=1"; Gas Inlet Radius=1/2"; Gas Train Extension=17 3/8"; Gas Train To Front=10 11/16"; Gas Train Vertical=19 1/8"; Gas Train to Left=4 3/8"; Gas Train to Rear=10 1/8"; Height to Cold Inlet=21 5/16"; Height to Hot Outlet 400-1500gal=78 1/2"; Hot Outlet Angle=0.00°; Hot Outlet Extension=34 1/2"; Hot Outlet Radius=1 1/2"; Hot Outlet Side 400-1500gal NPT=0"; Hot Outlet Side Extension=34 1/2"; Hot Outlet Top 250-400gal NPT=3"; Input=500000 Btu/h; Model=50 L 750A-TPX; Pump Extension=37 7/8"; Pump Line Radius=5/8"; Pump Line to Economizer Location=36 1/8"; Rear Cowling Extension=1"; Relief Angle 50-160 Prefix=45.00°; Relief Angle 75-160 Prefix=38.00°; Relief Extension=37 1/2"; Relief Extension 50-160 Prefix=37 1/2"; Relief Extension 75-160 Prefix=10"; Relief Height=77 11/16"; Relief NPT=3/4"; Relief Radius=3/8"; Shipping Weight lbs.=2770; Skid Length=93 5/8"; Skid Spacing=37"; Skid to Front=55 1/8"; Test Building Return Height=20 11/16"; Unit Height=93 9/16"; Unit Radius=33 1/2"; Vent Connection Housing Extension=8 13/16"; Vent Extension=36 7/8"; Vent Height=6 7/8"; Vent Location=4"
- 75 L 900A-TPX: 100 Prefix Recovery Rate 40F to 140F (gph)=-; 130 Prefix Recovery Rate 40F to 140F (gph)=-; 160 Prefix Recovery Rate 40F to 140F (gph)=-; 50 Prefix Recovery Rate 40F to 140F (gph)=-; 75 Prefix Recovery Rate 40F to 140F (gph)=881; Building Return Connection Height 50 (250-400gal only) prefix=1/2"; Building Return Connection Height 50-160 prefix=13 11/16"; Building Return Extension 250-400gal=1"; Building Return Extension 500-600gal=40 3/4"; Building Return Extension Angle 500-600gal=45.00°; Building Return Height=40"; Building Return Location=28 7/8"; Building Return NPT=1 1/2"; Building Return Radius=3/4"; Building Return to Economizer=14 1/16"; Burner Conn Height=88 9/16"; Burner Height=18 3/16"; Burner Housing -Y=18 7/16"; Burner Housing Extension=20"; Burner Housing to Left=7 1/4"; Burner Housing to Right=7 7/8"; Burner Nozzle Extension=12 3/8"; Cold Inlet Extension=38 3/8"; Cold Inlet NPT=3"; Cold Inlet Radius=1 1/2"; Combustion Air Connection X=15 7/16"; Combustion Air Connection to Right=3 9/16"; Condensate Extension=4 3/8"; Control Enclosure Angle=42.00°; Control Enclosure Location=41 5/16"; Control Panel Extension=40 1/2"; Drain Extension=35 1/8"; Drain NPT=1 1/2"; Drain Radius=3/4"; Economizer Connection Y=5 5/16"; Economizer Depth=10"; Economizer Inlet Outlet Connection Spacing=4"; Economizer Width=32"; Energy Height=33 11/16"; Flue Collector Extension=8 13/16"; Flue Collector Outlet to Front=3 11/16"; Flue Collector Radius=12 1/8"; Front Cowling Extension=41 1/4"; Gas Inlet NPT=1"; Gas Inlet Radius=1/2"; Gas Train Extension=17 3/8"; Gas Train To Front=11 5/8"; Gas Train Vertical=19 1/8"; Gas Train to Left=4 3/8"; Gas Train to Rear=10 11/16"; Height to Cold Inlet=21 5/16"; Height to Hot Outlet 400-1500gal=78 1/2"; Hot Outlet Angle=0.00°; Hot Outlet Extension=34 1/2"; Hot Outlet Radius=1 1/2"; Hot Outlet Side 400-1500gal NPT=0"; Hot Outlet Side Extension=34 1/2"; Hot Outlet Top 250-400gal NPT=3"; Input=750000 Btu/h; Model=75 L 900A-TPX; Pump Extension=37 7/8"; Pump Line Radius=5/8"; Pump Line to Economizer Location=36 1/8"; Rear Cowling Extension=1"; Relief Angle 50-160 Prefix=45.00°; Relief Angle 75-160 Prefix=38.00°; Relief Extension=37 1/2"; Relief Extension 50-160 Prefix=37 1/2"; Relief Extension 75-160 Prefix=39 1/2"; Relief Height=77 11/16"; Relief NPT=3/4"; Relief Radius=3/8"; Shipping Weight lbs.=2850; Skid Length=93 5/8"; Skid Spacing=37"; Skid to Front=55 1/8"; Test Building Return Height=20 11/16"; Unit Height=93 9/16"; Unit Radius=33 1/2"; Vent Connection Housing Extension=8 13/16"; Vent Extension=36 7/8"; Vent Height=6 7/8"; Vent Location=4"
- 100 L 900A-TPX: 100 Prefix Recovery Rate 40F to 140F (gph)=1175; 130 Prefix Recovery Rate 40F to 140F (gph)=-; 160 Prefix Recovery Rate 40F to 140F (gph)=-; 50 Prefix Recovery Rate 40F to 140F (gph)=-; 75 Prefix Recovery Rate 40F to 140F (gph)=-; Building Return Connection Height 50 (250-400gal only) prefix=1/2"; Building Return Connection Height 50-160 prefix=13 11/16"; Building Return Extension 250-400gal=1"; Building Return Extension 500-600gal=40 3/4"; Building Return Extension Angle 500-600gal=45.00°; Building Return Height=40"; Building Return Location=28 7/8"; Building Return NPT=1 1/2"; Building Return Radius=3/4"; Building Return to Economizer=14 1/16"; Burner Conn Height=88 9/16"; Burner Height=18 3/16"; Burner Housing -Y=18 7/16"; Burner Housing Extension=20"; Burner Housing to Left=7 1/4"; Burner Housing to Right=7 7/8"; Burner Nozzle Extension=12 3/8"; Cold Inlet Extension=38 3/8"; Cold Inlet NPT=3"; Cold Inlet Radius=1 1/2"; Combustion Air Connection X=15 7/16"; Combustion Air Connection to Right=3 9/16"; Condensate Extension=4 3/8"; Control Enclosure Angle=55.00°; Control Enclosure Location=41 5/16"; Control Panel Extension=40 1/2"; Drain Extension=35 1/8"; Drain NPT=1 1/2"; Drain Radius=3/4"; Economizer Connection Y=5 5/16"; Economizer Depth=10"; Economizer Inlet Outlet Connection Spacing=4"; Economizer Width=32"; Energy Height=33 11/16"; Flue Collector Extension=8 13/16"; Flue Collector Outlet to Front=3 11/16"; Flue Collector Radius=12 1/8"; Front Cowling Extension=41 1/4"; Gas Inlet NPT=1"; Gas Inlet Radius=1/2"; Gas Train Extension=17 3/8"; Gas Train To Front=11 5/8"; Gas Train Vertical=19 1/8"; Gas Train to Left=4 3/8"; Gas Train to Rear=10 11/16"; Height to Cold Inlet=21 5/16"; Height to Hot Outlet 400-1500gal=78 1/2"; Hot Outlet Angle=0.00°; Hot Outlet Extension=34 1/2"; Hot Outlet Radius=1 1/2"; Hot Outlet Side 400-1500gal NPT=0"; Hot Outlet Side Extension=34 1/2"; Hot Outlet Top 250-400gal NPT=3"; Input=1000000 Btu/h; Model=100 L 900A-TPX; Pump Extension=37 7/8"; Pump Line Radius=5/8"; Pump Line to Economizer Location=36 1/8"; Rear Cowling Extension=1"; Relief Angle 50-160 Prefix=45.00°; Relief Angle 75-160 Prefix=38.00°; Relief Extension=37 1/2"; Relief Extension 50-160 Prefix=37 1/2"; Relief Extension 75-160 Prefix=39 1/2"; Relief Height=77 11/16"; Relief NPT=3/4"; Relief Radius=3/8"; Shipping Weight lbs.=2890; Skid Length=93 5/8"; Skid Spacing=37"; Skid to Front=55 1/8"; Test Building Return Height=20 11/16"; Unit Height=93 9/16"; Unit Radius=33 1/2"; Vent Connection Housing Extension=8 13/16"; Vent Extension=36 7/8"; Vent Height=6 7/8"; Vent Location=4"
- 130 L 900A-TPX: 100 Prefix Recovery Rate 40F to 140F (gph)=-; 130 Prefix Recovery Rate 40F to 140F (gph)=1527; 160 Prefix Recovery Rate 40F to 140F (gph)=-; 50 Prefix Recovery Rate 40F to 140F (gph)=-; 75 Prefix Recovery Rate 40F to 140F (gph)=-; Building Return Connection Height 50 (250-400gal only) prefix=1/2"; Building Return Connection Height 50-160 prefix=14 3/8"; Building Return Extension 250-400gal=1"; Building Return Extension 500-600gal=40 7/8"; Building Return Extension Angle 500-600gal=45.00°; Building Return Height=40"; Building Return Location=28 7/8"; Building Return NPT=2"; Building Return Radius=1"; Building Return to Economizer=27 7/8"; Burner Conn Height=88 9/16"; Burner Height=18"; Burner Housing -Y=19 7/16"; Burner Housing Extension=24 1/4"; Burner Housing to Left=7 1/4"; Burner Housing to Right=11 1/2"; Burner Nozzle Extension=16 3/4"; Cold Inlet Extension=38 7/8"; Cold Inlet NPT=3"; Cold Inlet Radius=1 1/2"; Combustion Air Connection X=15 7/16"; Combustion Air Connection to Right=3 9/16"; Condensate Extension=4 3/16"; Control Enclosure Angle=42.00°; Control Enclosure Location=41 5/16"; Control Panel Extension=40 1/2"; Drain Extension=35 1/8"; Drain NPT=1 1/2"; Drain Radius=3/4"; Economizer Connection Y=5"; Economizer Depth=18"; Economizer Inlet Outlet Connection Spacing=7"; Economizer Width=32 3/4"; Energy Height=33 11/16"; Flue Collector Extension=13 1/4"; Flue Collector Outlet to Front=6 5/8"; Flue Collector Radius=11 13/16"; Front Cowling Extension=53 5/8"; Gas Inlet NPT=1"; Gas Inlet Radius=1/2"; Gas Train Extension=19 3/8"; Gas Train To Front=11 5/8"; Gas Train Vertical=24"; Gas Train to Left=6 5/8"; Gas Train to Rear=10 11/16"; Height to Cold Inlet=21 5/16"; Height to Hot Outlet 400-1500gal=78 1/2"; Hot Outlet Angle=0.00°; Hot Outlet Extension=34 1/2"; Hot Outlet Radius=1 1/2"; Hot Outlet Side 400-1500gal NPT=0"; Hot Outlet Side Extension=34 1/2"; Hot Outlet Top 250-400gal NPT=3"; Input=1300000 Btu/h; Model=130 L 900A-TPX; Pump Extension=37 7/8"; Pump Line Radius=1"; Pump Line to Economizer Location=36 5/16"; Rear Cowling Extension=1"; Relief Angle 50-160 Prefix=45.00°; Relief Angle 75-160 Prefix=38.00°; Relief Extension=37 1/2"; Relief Extension 50-160 Prefix=37 1/2"; Relief Extension 75-160 Prefix=39 1/2"; Relief Height=77 11/16"; Relief NPT=3/4"; Relief Radius=3/8"; Shipping Weight lbs.=3130; Skid Length=113"; Skid Spacing=37"; Skid to Front=74 3/4"; Test Building Return Height=20 11/16"; Unit Height=93 9/16"; Unit Radius=33 1/2"; Vent Connection Housing Extension=8 13/16"; Vent Extension=36 7/8"; Vent Height=7 1/4"; Vent Location=4 11/16"
- 160 L 900A-TPX: 100 Prefix Recovery Rate 40F to 140F (gph)=-; 130 Prefix Recovery Rate 40F to 140F (gph)=-; 160 Prefix Recovery Rate 40F to 140F (gph)=1880; 50 Prefix Recovery Rate 40F to 140F (gph)=-; 75 Prefix Recovery Rate 40F to 140F (gph)=-; Building Return Connection Height 50 (250-400gal only) prefix=1/2"; Building Return Connection Height 50-160 prefix=14 3/8"; Building Return Extension 250-400gal=1"; Building Return Extension 500-600gal=40 7/8"; Building Return Extension Angle 500-600gal=45.00°; Building Return Height=40"; Building Return Location=28 7/8"; Building Return NPT=2"; Building Return Radius=1"; Building Return to Economizer=27 7/8"; Burner Conn Height=88 9/16"; Burner Height=18"; Burner Housing -Y=19 7/16"; Burner Housing Extension=24 1/4"; Burner Housing to Left=7 1/4"; Burner Housing to Right=11 1/2"; Burner Nozzle Extension=16 3/4"; Cold Inlet Extension=38 7/8"; Cold Inlet NPT=3"; Cold Inlet Radius=1 1/2"; Combustion Air Connection X=15 7/16"; Combustion Air Connection to Right=3 9/16"; Condensate Extension=4 3/16"; Control Enclosure Angle=42.00°; Control Enclosure Location=41 5/16"; Control Panel Extension=40 1/2"; Drain Extension=35 1/8"; Drain NPT=1 1/2"; Drain Radius=3/4"; Economizer Connection Y=5"; Economizer Depth=18"; Economizer Inlet Outlet Connection Spacing=7"; Economizer Width=32 3/4"; Energy Height=33 11/16"; Flue Collector Extension=13 1/4"; Flue Collector Outlet to Front=6 5/8"; Flue Collector Radius=12 1/8"; Front Cowling Extension=53 5/8"; Gas Inlet NPT=1"; Gas Inlet Radius=1/2"; Gas Train Extension=19 3/8"; Gas Train To Front=11 5/8"; Gas Train Vertical=24"; Gas Train to Left=6 5/8"; Gas Train to Rear=10 11/16"; Height to Cold Inlet=21 5/16"; Height to Hot Outlet 400-1500gal=78 1/2"; Hot Outlet Angle=0.00°; Hot Outlet Extension=34 1/2"; Hot Outlet Radius=1 1/2"; Hot Outlet Side 400-1500gal NPT=0"; Hot Outlet Side Extension=34 1/2"; Hot Outlet Top 250-400gal NPT=3"; Input=1600000 Btu/h; Model=160 L 900A-TPX; Pump Extension=37 7/8"; Pump Line Radius=1"; Pump Line to Economizer Location=36 5/16"; Rear Cowling Extension=1"; Relief Angle 50-160 Prefix=45.00°; Relief Angle 75-160 Prefix=38.00°; Relief Extension=37 1/2"; Relief Extension 50-160 Prefix=37 1/2"; Relief Extension 75-160 Prefix=39 1/2"; Relief Height=77 11/16"; Relief NPT=3/4"; Relief Radius=3/8"; Shipping Weight lbs.=3130; Skid Length=113"; Skid Spacing=37"; Skid to Front=74 3/4"; Test Building Return Height=20 11/16"; Unit Height=93 9/16"; Unit Radius=33 1/2"; Vent Connection Housing Extension=8 13/16"; Vent Extension=36 7/8"; Vent Height=7 1/4"; Vent Location=4 11/16"
- 50 L 1000A-TPX: 100 Prefix Recovery Rate 40F to 140F (gph)=-; 130 Prefix Recovery Rate 40F to 140F (gph)=-; 160 Prefix Recovery Rate 40F to 140F (gph)=-; 50 Prefix Recovery Rate 40F to 140F (gph)=587; 75 Prefix Recovery Rate 40F to 140F (gph)=-; Building Return Connection Height 50 (250-400gal only) prefix=1/2"; Building Return Connection Height 50-160 prefix=13 11/16"; Building Return Extension 250-400gal=1"; Building Return Extension 500-600gal=46 3/8"; Building Return Extension Angle 500-600gal=51.38°; Building Return Height=40"; Building Return Location=28 7/8"; Building Return NPT=1 1/2"; Building Return Radius=3/4"; Building Return to Economizer=13"; Burner Conn Height=77 1/8"; Burner Height=18 3/16"; Burner Housing -Y=15 5/8"; Burner Housing Extension=19"; Burner Housing to Left=5 3/16"; Burner Housing to Right=7 1/4"; Burner Nozzle Extension=12 3/8"; Cold Inlet Extension=43 5/16"; Cold Inlet NPT=3"; Cold Inlet Radius=1 1/2"; Combustion Air Connection X=15 7/16"; Combustion Air Connection to Right=3 9/16"; Condensate Extension=4 3/8"; Control Enclosure Angle=41.00°; Control Enclosure Location=41 5/16"; Control Panel Extension=44 7/16"; Drain Extension=39 1/16"; Drain NPT=1 1/2"; Drain Radius=3/4"; Economizer Connection Y=5 5/16"; Economizer Depth=10"; Economizer Inlet Outlet Connection Spacing=4"; Economizer Width=32"; Energy Height=33 11/16"; Flue Collector Extension=8 13/16"; Flue Collector Outlet to Front=3 11/16"; Flue Collector Radius=12 1/8"; Front Cowling Extension=47 7/16"; Gas Inlet NPT=1"; Gas Inlet Radius=1/2"; Gas Train Extension=17 3/8"; Gas Train To Front=10 11/16"; Gas Train Vertical=19 1/8"; Gas Train to Left=4 3/8"; Gas Train to Rear=10 1/8"; Height to Cold Inlet=21 5/16"; Height to Hot Outlet 400-1500gal=67 1/2"; Hot Outlet Angle=0.00°; Hot Outlet Extension=38 7/16"; Hot Outlet Radius=1 1/2"; Hot Outlet Side 400-1500gal NPT=0"; Hot Outlet Side Extension=38 7/16"; Hot Outlet Top 250-400gal NPT=3"; Input=500000 Btu/h; Model=50 L 1000A-TPX; Pump Extension=41 13/16"; Pump Line Radius=5/8"; Pump Line to Economizer Location=41 1/16"; Rear Cowling Extension=1"; Relief Angle 50-160 Prefix=51.38°; Relief Angle 75-160 Prefix=45.00°; Relief Extension=41 7/16"; Relief Extension 50-160 Prefix=41 7/16"; Relief Extension 75-160 Prefix=10"; Relief Height=66 1/4"; Relief NPT=3/4"; Relief Radius=3/8"; Shipping Weight lbs.=3600; Skid Length=104"; Skid Spacing=44"; Skid to Front=61 9/16"; Test Building Return Height=20 11/16"; Unit Height=82 1/8"; Unit Radius=37 7/16"; Vent Connection Housing Extension=8 13/16"; Vent Extension=40 13/16"; Vent Height=6 7/8"; Vent Location=4"
- 75 L 1000A-TPX: 100 Prefix Recovery Rate 40F to 140F (gph)=-; 130 Prefix Recovery Rate 40F to 140F (gph)=-; 160 Prefix Recovery Rate 40F to 140F (gph)=-; 50 Prefix Recovery Rate 40F to 140F (gph)=-; 75 Prefix Recovery Rate 40F to 140F (gph)=881; Building Return Connection Height 50 (250-400gal only) prefix=1/2"; Building Return Connection Height 50-160 prefix=13 11/16"; Building Return Extension 250-400gal=1"; Building Return Extension 500-600gal=46 3/8"; Building Return Extension Angle 500-600gal=51.38°; Building Return Height=40"; Building Return Location=28 7/8"; Building Return NPT=1 1/2"; Building Return Radius=3/4"; Building Return to Economizer=13"; Burner Conn Height=77 1/8"; Burner Height=18 3/16"; Burner Housing -Y=18 7/16"; Burner Housing Extension=20"; Burner Housing to Left=7 1/4"; Burner Housing to Right=7 7/8"; Burner Nozzle Extension=12 3/8"; Cold Inlet Extension=43 5/16"; Cold Inlet NPT=3"; Cold Inlet Radius=1 1/2"; Combustion Air Connection X=15 7/16"; Combustion Air Connection to Right=3 9/16"; Condensate Extension=4 3/8"; Control Enclosure Angle=41.00°; Control Enclosure Location=41 5/16"; Control Panel Extension=44 7/16"; Drain Extension=39 1/16"; Drain NPT=1 1/2"; Drain Radius=3/4"; Economizer Connection Y=5 5/16"; Economizer Depth=10"; Economizer Inlet Outlet Connection Spacing=4"; Economizer Width=32"; Energy Height=33 11/16"; Flue Collector Extension=8 13/16"; Flue Collector Outlet to Front=3 11/16"; Flue Collector Radius=12 1/8"; Front Cowling Extension=47 7/16"; Gas Inlet NPT=1"; Gas Inlet Radius=1/2"; Gas Train Extension=17 3/8"; Gas Train To Front=11 5/8"; Gas Train Vertical=20 5/8"; Gas Train to Left=4 3/8"; Gas Train to Rear=10 11/16"; Height to Cold Inlet=21 5/16"; Height to Hot Outlet 400-1500gal=67 1/2"; Hot Outlet Angle=0.00°; Hot Outlet Extension=38 7/16"; Hot Outlet Radius=1 1/2"; Hot Outlet Side 400-1500gal NPT=0"; Hot Outlet Side Extension=38 7/16"; Hot Outlet Top 250-400gal NPT=3"; Input=750000 Btu/h; Model=75 L 1000A-TPX; Pump Extension=41 13/16"; Pump Line Radius=5/8"; Pump Line to Economizer Location=41 1/16"; Rear Cowling Extension=1"; Relief Angle 50-160 Prefix=51.38°; Relief Angle 75-160 Prefix=45.00°; Relief Extension=41 7/16"; Relief Extension 50-160 Prefix=41 7/16"; Relief Extension 75-160 Prefix=43 7/16"; Relief Height=66 1/4"; Relief NPT=3/4"; Relief Radius=3/8"; Shipping Weight lbs.=3700; Skid Length=104"; Skid Spacing=44"; Skid to Front=61 9/16"; Test Building Return Height=20 11/16"; Unit Height=82 1/8"; Unit Radius=37 7/16"; Vent Connection Housing Extension=8 13/16"; Vent Extension=40 13/16"; Vent Height=6 7/8"; Vent Location=4"
- 100 L 1000A-TPX: 100 Prefix Recovery Rate 40F to 140F (gph)=1175; 130 Prefix Recovery Rate 40F to 140F (gph)=-; 160 Prefix Recovery Rate 40F to 140F (gph)=-; 50 Prefix Recovery Rate 40F to 140F (gph)=-; 75 Prefix Recovery Rate 40F to 140F (gph)=-; Building Return Connection Height 50 (250-400gal only) prefix=1/2"; Building Return Connection Height 50-160 prefix=13 11/16"; Building Return Extension 250-400gal=1"; Building Return Extension 500-600gal=46 3/8"; Building Return Extension Angle 500-600gal=51.38°; Building Return Height=40"; Building Return Location=28 7/8"; Building Return NPT=1 1/2"; Building Return Radius=3/4"; Building Return to Economizer=13"; Burner Conn Height=77 1/8"; Burner Height=18 3/16"; Burner Housing -Y=18 7/16"; Burner Housing Extension=20"; Burner Housing to Left=7 1/4"; Burner Housing to Right=7 7/8"; Burner Nozzle Extension=12 3/8"; Cold Inlet Extension=43 5/16"; Cold Inlet NPT=3"; Cold Inlet Radius=1 1/2"; Combustion Air Connection X=15 7/16"; Combustion Air Connection to Right=3 9/16"; Condensate Extension=4 3/8"; Control Enclosure Angle=41.00°; Control Enclosure Location=41 5/16"; Control Panel Extension=44 7/16"; Drain Extension=39 1/16"; Drain NPT=1 1/2"; Drain Radius=3/4"; Economizer Connection Y=5 5/16"; Economizer Depth=10"; Economizer Inlet Outlet Connection Spacing=4"; Economizer Width=32"; Energy Height=33 11/16"; Flue Collector Extension=8 13/16"; Flue Collector Outlet to Front=3 11/16"; Flue Collector Radius=12 1/8"; Front Cowling Extension=47 7/16"; Gas Inlet NPT=1"; Gas Inlet Radius=1/2"; Gas Train Extension=17 3/8"; Gas Train To Front=11 5/8"; Gas Train Vertical=20 5/8"; Gas Train to Left=4 3/8"; Gas Train to Rear=10 11/16"; Height to Cold Inlet=21 5/16"; Height to Hot Outlet 400-1500gal=67 1/2"; Hot Outlet Angle=45.00°; Hot Outlet Extension=38 7/16"; Hot Outlet Radius=1 1/2"; Hot Outlet Side 400-1500gal NPT=0"; Hot Outlet Side Extension=38 7/16"; Hot Outlet Top 250-400gal NPT=3"; Input=1000000 Btu/h; Model=100 L 1000A-TPX; Pump Extension=41 13/16"; Pump Line Radius=5/8"; Pump Line to Economizer Location=41 1/16"; Rear Cowling Extension=1"; Relief Angle 50-160 Prefix=51.38°; Relief Angle 75-160 Prefix=45.00°; Relief Extension=41 7/16"; Relief Extension 50-160 Prefix=41 7/16"; Relief Extension 75-160 Prefix=43 7/16"; Relief Height=66 1/4"; Relief NPT=3/4"; Relief Radius=3/8"; Shipping Weight lbs.=3720; Skid Length=104"; Skid Spacing=44"; Skid to Front=61 9/16"; Test Building Return Height=20 11/16"; Unit Height=82 1/8"; Unit Radius=37 7/16"; Vent Connection Housing Extension=8 13/16"; Vent Extension=40 13/16"; Vent Height=6 7/8"; Vent Location=4"
- 130 L 1000A-TPX: 100 Prefix Recovery Rate 40F to 140F (gph)=-; 130 Prefix Recovery Rate 40F to 140F (gph)=1527; 160 Prefix Recovery Rate 40F to 140F (gph)=-; 50 Prefix Recovery Rate 40F to 140F (gph)=-; 75 Prefix Recovery Rate 40F to 140F (gph)=-; Building Return Connection Height 50 (250-400gal only) prefix=1/2"; Building Return Connection Height 50-160 prefix=13 11/16"; Building Return Extension 250-400gal=1"; Building Return Extension 500-600gal=46 19/32"; Building Return Extension Angle 500-600gal=52.00°; Building Return Height=40"; Building Return Location=28 7/8"; Building Return NPT=2"; Building Return Radius=1"; Building Return to Economizer=15 3/16"; Burner Conn Height=77 1/8"; Burner Height=18 3/16"; Burner Housing -Y=18 7/16"; Burner Housing Extension=20"; Burner Housing to Left=7 1/4"; Burner Housing to Right=7 7/8"; Burner Nozzle Extension=12 3/8"; Cold Inlet Extension=43 3/4"; Cold Inlet NPT=3"; Cold Inlet Radius=1 1/2"; Combustion Air Connection X=15 7/16"; Combustion Air Connection to Right=3 9/16"; Condensate Extension=4 3/8"; Control Enclosure Angle=41.00°; Control Enclosure Location=41 5/16"; Control Panel Extension=44 7/16"; Drain Extension=39 1/16"; Drain NPT=1 1/2"; Drain Radius=3/4"; Economizer Connection Y=5 5/16"; Economizer Depth=10"; Economizer Inlet Outlet Connection Spacing=4"; Economizer Width=32"; Energy Height=33 11/16"; Flue Collector Extension=13 1/2"; Flue Collector Outlet to Front=6 5/8"; Flue Collector Radius=11 13/16"; Front Cowling Extension=47 1/2"; Gas Inlet NPT=1"; Gas Inlet Radius=1/2"; Gas Train Extension=19 3/8"; Gas Train To Front=11 5/8"; Gas Train Vertical=24"; Gas Train to Left=6 5/8"; Gas Train to Rear=10 11/16"; Height to Cold Inlet=21 5/16"; Height to Hot Outlet 400-1500gal=67 1/2"; Hot Outlet Angle=0.00°; Hot Outlet Extension=38 7/16"; Hot Outlet Radius=1 1/2"; Hot Outlet Side 400-1500gal NPT=0"; Hot Outlet Side Extension=38 7/16"; Hot Outlet Top 250-400gal NPT=3"; Input=1300000 Btu/h; Model=130 L 1000A-TPX; Pump Extension=41 13/16"; Pump Line Radius=1"; Pump Line to Economizer Location=41 1/4"; Rear Cowling Extension=1"; Relief Angle 50-160 Prefix=51.38°; Relief Angle 75-160 Prefix=45.00°; Relief Extension=41 7/16"; Relief Extension 50-160 Prefix=41 7/16"; Relief Extension 75-160 Prefix=43 7/16"; Relief Height=66 1/4"; Relief NPT=3/4"; Relief Radius=3/8"; Shipping Weight lbs.=3950; Skid Length=111 1/2"; Skid Spacing=44"; Skid to Front=68 13/16"; Test Building Return Height=20 11/16"; Unit Height=82 1/8"; Unit Radius=37 7/16"; Vent Connection Housing Extension=8 13/16"; Vent Extension=40 13/16"; Vent Height=7 1/4"; Vent Location=4 11/16"
- 160 L 1000A-TPX: 100 Prefix Recovery Rate 40F to 140F (gph)=-; 130 Prefix Recovery Rate 40F to 140F (gph)=-; 160 Prefix Recovery Rate 40F to 140F (gph)=1880; 50 Prefix Recovery Rate 40F to 140F (gph)=-; 75 Prefix Recovery Rate 40F to 140F (gph)=-; Building Return Connection Height 50 (250-400gal only) prefix=1/2"; Building Return Connection Height 50-160 prefix=13 11/16"; Building Return Extension 250-400gal=1"; Building Return Extension 500-600gal=46 19/32"; Building Return Extension Angle 500-600gal=52.00°; Building Return Height=40"; Building Return Location=28 7/8"; Building Return NPT=2"; Building Return Radius=1"; Building Return to Economizer=15 3/16"; Burner Conn Height=77 1/8"; Burner Height=18 3/16"; Burner Housing -Y=18 7/16"; Burner Housing Extension=20"; Burner Housing to Left=7 1/4"; Burner Housing to Right=7 7/8"; Burner Nozzle Extension=12 3/8"; Cold Inlet Extension=43 3/4"; Cold Inlet NPT=3"; Cold Inlet Radius=1 1/2"; Combustion Air Connection X=15 7/16"; Combustion Air Connection to Right=3 9/16"; Condensate Extension=4 3/8"; Control Enclosure Angle=41.00°; Control Enclosure Location=41 5/16"; Control Panel Extension=44 7/16"; Drain Extension=39 1/16"; Drain NPT=1 1/2"; Drain Radius=3/4"; Economizer Connection Y=5 5/16"; Economizer Depth=10"; Economizer Inlet Outlet Connection Spacing=4"; Economizer Width=32"; Energy Height=33 11/16"; Flue Collector Extension=13 1/2"; Flue Collector Outlet to Front=6 5/8"; Flue Collector Radius=11 13/16"; Front Cowling Extension=47 1/2"; Gas Inlet NPT=1"; Gas Inlet Radius=1/2"; Gas Train Extension=19 3/8"; Gas Train To Front=11 5/8"; Gas Train Vertical=24"; Gas Train to Left=6 5/8"; Gas Train to Rear=10 11/16"; Height to Cold Inlet=21 5/16"; Height to Hot Outlet 400-1500gal=67 1/2"; Hot Outlet Angle=0.00°; Hot Outlet Extension=38 7/16"; Hot Outlet Radius=1 1/2"; Hot Outlet Side 400-1500gal NPT=0"; Hot Outlet Side Extension=38 7/16"; Hot Outlet Top 250-400gal NPT=3"; Input=1600000 Btu/h; Model=160 L 1000A-TPX; Pump Extension=41 13/16"; Pump Line Radius=1"; Pump Line to Economizer Location=41 1/4"; Rear Cowling Extension=1"; Relief Angle 50-160 Prefix=51.38°; Relief Angle 75-160 Prefix=45.00°; Relief Extension=41 7/16"; Relief Extension 50-160 Prefix=41 7/16"; Relief Extension 75-160 Prefix=43 7/16"; Relief Height=66 1/4"; Relief NPT=3/4"; Relief Radius=3/8"; Shipping Weight lbs.=3960; Skid Length=111 1/2"; Skid Spacing=44"; Skid to Front=65 13/16"; Test Building Return Height=20 11/16"; Unit Height=82 1/8"; Unit Radius=37 7/16"; Vent Connection Housing Extension=8 13/16"; Vent Extension=40 13/16"; Vent Height=7 1/4"; Vent Location=4 11/16"
- 50 L 1250A-TPX: 100 Prefix Recovery Rate 40F to 140F (gph)=-; 130 Prefix Recovery Rate 40F to 140F (gph)=-; 160 Prefix Recovery Rate 40F to 140F (gph)=-; 50 Prefix Recovery Rate 40F to 140F (gph)=587; 75 Prefix Recovery Rate 40F to 140F (gph)=-; Building Return Connection Height 50 (250-400gal only) prefix=1/2"; Building Return Connection Height 50-160 prefix=13 11/16"; Building Return Extension 250-400gal=1"; Building Return Extension 500-600gal=46 3/8"; Building Return Extension Angle 500-600gal=51.38°; Building Return Height=40"; Building Return Location=28 7/8"; Building Return NPT=1 1/2"; Building Return Radius=3/4"; Building Return to Economizer=13"; Burner Conn Height=89 1/8"; Burner Height=18 3/16"; Burner Housing -Y=15 5/8"; Burner Housing Extension=19"; Burner Housing to Left=5 3/16"; Burner Housing to Right=7 1/4"; Burner Nozzle Extension=12 3/8"; Cold Inlet Extension=43 5/16"; Cold Inlet NPT=3"; Cold Inlet Radius=1 1/2"; Combustion Air Connection X=15 7/16"; Combustion Air Connection to Right=3 9/16"; Condensate Extension=4 3/8"; Control Enclosure Angle=41.00°; Control Enclosure Location=41 5/16"; Control Panel Extension=44 7/16"; Drain Extension=39 1/16"; Drain NPT=1 1/2"; Drain Radius=3/4"; Economizer Connection Y=5 5/16"; Economizer Depth=10"; Economizer Inlet Outlet Connection Spacing=4"; Economizer Width=32"; Energy Height=33 11/16"; Flue Collector Extension=8 13/16"; Flue Collector Outlet to Front=3 11/16"; Flue Collector Radius=12 1/8"; Front Cowling Extension=47 7/16"; Gas Inlet NPT=1"; Gas Inlet Radius=1/2"; Gas Train Extension=17 3/8"; Gas Train To Front=10 11/16"; Gas Train Vertical=19 1/8"; Gas Train to Left=4 3/8"; Gas Train to Rear=10 1/8"; Height to Cold Inlet=21 5/16"; Height to Hot Outlet 400-1500gal=79 1/2"; Hot Outlet Angle=0.00°; Hot Outlet Extension=38 7/16"; Hot Outlet Radius=1 1/2"; Hot Outlet Side 400-1500gal NPT=0"; Hot Outlet Side Extension=38 7/16"; Hot Outlet Top 250-400gal NPT=3"; Input=500000 Btu/h; Model=50 L 1250A-TPX; Pump Extension=41 13/16"; Pump Line Radius=5/8"; Pump Line to Economizer Location=41 1/16"; Rear Cowling Extension=1"; Relief Angle 50-160 Prefix=51.38°; Relief Angle 75-160 Prefix=45.00°; Relief Extension=41 7/16"; Relief Extension 50-160 Prefix=41 7/16"; Relief Extension 75-160 Prefix=10"; Relief Height=78 1/4"; Relief NPT=3/4"; Relief Radius=3/8"; Shipping Weight lbs.=3830; Skid Length=104"; Skid Spacing=44"; Skid to Front=61 9/16"; Test Building Return Height=20 11/16"; Unit Height=94 1/8"; Unit Radius=37 7/16"; Vent Connection Housing Extension=8 13/16"; Vent Extension=40 13/16"; Vent Height=6 7/8"; Vent Location=4"
- 75 L 1250A-TPX: 100 Prefix Recovery Rate 40F to 140F (gph)=-; 130 Prefix Recovery Rate 40F to 140F (gph)=-; 160 Prefix Recovery Rate 40F to 140F (gph)=-; 50 Prefix Recovery Rate 40F to 140F (gph)=-; 75 Prefix Recovery Rate 40F to 140F (gph)=881; Building Return Connection Height 50 (250-400gal only) prefix=1/2"; Building Return Connection Height 50-160 prefix=13 11/16"; Building Return Extension 250-400gal=1"; Building Return Extension 500-600gal=46 3/8"; Building Return Extension Angle 500-600gal=51.38°; Building Return Height=40"; Building Return Location=28 7/8"; Building Return NPT=1 1/2"; Building Return Radius=3/4"; Building Return to Economizer=13"; Burner Conn Height=89 1/8"; Burner Height=18 3/16"; Burner Housing -Y=18 7/16"; Burner Housing Extension=20"; Burner Housing to Left=7 1/4"; Burner Housing to Right=7 7/8"; Burner Nozzle Extension=12 3/8"; Cold Inlet Extension=43 5/16"; Cold Inlet NPT=3"; Cold Inlet Radius=1 1/2"; Combustion Air Connection X=15 7/16"; Combustion Air Connection to Right=3 9/16"; Condensate Extension=4 3/8"; Control Enclosure Angle=41.00°; Control Enclosure Location=41 5/16"; Control Panel Extension=44 7/16"; Drain Extension=39 1/16"; Drain NPT=1 1/2"; Drain Radius=3/4"; Economizer Connection Y=5 5/16"; Economizer Depth=10"; Economizer Inlet Outlet Connection Spacing=4"; Economizer Width=32"; Energy Height=33 11/16"; Flue Collector Extension=8 13/16"; Flue Collector Outlet to Front=3 11/16"; Flue Collector Radius=12 1/8"; Front Cowling Extension=47 7/16"; Gas Inlet NPT=1"; Gas Inlet Radius=1/2"; Gas Train Extension=17 3/8"; Gas Train To Front=11 5/8"; Gas Train Vertical=20 5/8"; Gas Train to Left=4 3/8"; Gas Train to Rear=10 11/16"; Height to Cold Inlet=21 5/16"; Height to Hot Outlet 400-1500gal=79 1/2"; Hot Outlet Angle=0.00°; Hot Outlet Extension=38 7/16"; Hot Outlet Radius=1 1/2"; Hot Outlet Side 400-1500gal NPT=0"; Hot Outlet Side Extension=38 7/16"; Hot Outlet Top 250-400gal NPT=3"; Input=750000 Btu/h; Model=75 L 1250A-TPX; Pump Extension=41 13/16"; Pump Line Radius=5/8"; Pump Line to Economizer Location=41 1/16"; Rear Cowling Extension=1"; Relief Angle 50-160 Prefix=51.38°; Relief Angle 75-160 Prefix=45.00°; Relief Extension=41 7/16"; Relief Extension 50-160 Prefix=41 7/16"; Relief Extension 75-160 Prefix=43 7/16"; Relief Height=78 1/4"; Relief NPT=3/4"; Relief Radius=3/8"; Shipping Weight lbs.=3910; Skid Length=104"; Skid Spacing=44"; Skid to Front=61 9/16"; Test Building Return Height=20 11/16"; Unit Height=94 1/8"; Unit Radius=37 7/16"; Vent Connection Housing Extension=8 13/16"; Vent Extension=40 13/16"; Vent Height=6 7/8"; Vent Location=4"
- 100 L 1250A-TPX: 100 Prefix Recovery Rate 40F to 140F (gph)=1175; 130 Prefix Recovery Rate 40F to 140F (gph)=-; 160 Prefix Recovery Rate 40F to 140F (gph)=-; 50 Prefix Recovery Rate 40F to 140F (gph)=-; 75 Prefix Recovery Rate 40F to 140F (gph)=-; Building Return Connection Height 50 (250-400gal only) prefix=1/2"; Building Return Connection Height 50-160 prefix=13 11/16"; Building Return Extension 250-400gal=1"; Building Return Extension 500-600gal=46 3/8"; Building Return Extension Angle 500-600gal=51.38°; Building Return Height=40"; Building Return Location=28 7/8"; Building Return NPT=1 1/2"; Building Return Radius=3/4"; Building Return to Economizer=13"; Burner Conn Height=89 1/8"; Burner Height=18 3/16"; Burner Housing -Y=18 7/16"; Burner Housing Extension=20"; Burner Housing to Left=7 1/4"; Burner Housing to Right=7 7/8"; Burner Nozzle Extension=12 3/8"; Cold Inlet Extension=43 5/16"; Cold Inlet NPT=3"; Cold Inlet Radius=1 1/2"; Combustion Air Connection X=15 7/16"; Combustion Air Connection to Right=3 9/16"; Condensate Extension=4 3/8"; Control Enclosure Angle=41.00°; Control Enclosure Location=41 5/16"; Control Panel Extension=44 7/16"; Drain Extension=39 1/16"; Drain NPT=1 1/2"; Drain Radius=3/4"; Economizer Connection Y=5 5/16"; Economizer Depth=10"; Economizer Inlet Outlet Connection Spacing=4"; Economizer Width=32"; Energy Height=33 11/16"; Flue Collector Extension=8 13/16"; Flue Collector Outlet to Front=3 11/16"; Flue Collector Radius=12 1/8"; Front Cowling Extension=47 7/16"; Gas Inlet NPT=1"; Gas Inlet Radius=1/2"; Gas Train Extension=17 3/8"; Gas Train To Front=11 5/8"; Gas Train Vertical=20 5/8"; Gas Train to Left=4 3/8"; Gas Train to Rear=10 11/16"; Height to Cold Inlet=21 5/16"; Height to Hot Outlet 400-1500gal=79 1/2"; Hot Outlet Angle=45.00°; Hot Outlet Extension=38 7/16"; Hot Outlet Radius=1 1/2"; Hot Outlet Side 400-1500gal NPT=0"; Hot Outlet Side Extension=38 7/16"; Hot Outlet Top 250-400gal NPT=3"; Input=1000000 Btu/h; Model=100 L 1250A-TPX; Pump Extension=41 13/16"; Pump Line Radius=5/8"; Pump Line to Economizer Location=41 1/16"; Rear Cowling Extension=1"; Relief Angle 50-160 Prefix=51.38°; Relief Angle 75-160 Prefix=45.00°; Relief Extension=41 7/16"; Relief Extension 50-160 Prefix=41 7/16"; Relief Extension 75-160 Prefix=43 7/16"; Relief Height=78 1/4"; Relief NPT=3/4"; Relief Radius=3/8"; Shipping Weight lbs.=3950; Skid Length=104"; Skid Spacing=44"; Skid to Front=61 9/16"; Test Building Return Height=20 11/16"; Unit Height=94 1/8"; Unit Radius=37 7/16"; Vent Connection Housing Extension=8 13/16"; Vent Extension=40 13/16"; Vent Height=6 7/8"; Vent Location=4"
- 130 L 1250A-TPX: 100 Prefix Recovery Rate 40F to 140F (gph)=-; 130 Prefix Recovery Rate 40F to 140F (gph)=1527; 160 Prefix Recovery Rate 40F to 140F (gph)=-; 50 Prefix Recovery Rate 40F to 140F (gph)=-; 75 Prefix Recovery Rate 40F to 140F (gph)=-; Building Return Connection Height 50 (250-400gal only) prefix=1/2"; Building Return Connection Height 50-160 prefix=13 11/16"; Building Return Extension 250-400gal=1"; Building Return Extension 500-600gal=46 19/32"; Building Return Extension Angle 500-600gal=52.00°; Building Return Height=40"; Building Return Location=28 7/8"; Building Return NPT=2"; Building Return Radius=1"; Building Return to Economizer=15 3/16"; Burner Conn Height=89 1/8"; Burner Height=18 3/16"; Burner Housing -Y=18 7/16"; Burner Housing Extension=20"; Burner Housing to Left=7 1/4"; Burner Housing to Right=7 7/8"; Burner Nozzle Extension=12 3/8"; Cold Inlet Extension=43 3/4"; Cold Inlet NPT=3"; Cold Inlet Radius=1 1/2"; Combustion Air Connection X=15 7/16"; Combustion Air Connection to Right=3 9/16"; Condensate Extension=4 3/8"; Control Enclosure Angle=41.00°; Control Enclosure Location=41 5/16"; Control Panel Extension=44 7/16"; Drain Extension=39 1/16"; Drain NPT=1 1/2"; Drain Radius=3/4"; Economizer Connection Y=5 5/16"; Economizer Depth=10"; Economizer Inlet Outlet Connection Spacing=4"; Economizer Width=32"; Energy Height=33 11/16"; Flue Collector Extension=13 1/2"; Flue Collector Outlet to Front=6 5/8"; Flue Collector Radius=11 13/16"; Front Cowling Extension=47 1/2"; Gas Inlet NPT=1"; Gas Inlet Radius=1/2"; Gas Train Extension=19 3/8"; Gas Train To Front=11 5/8"; Gas Train Vertical=24"; Gas Train to Left=6 5/8"; Gas Train to Rear=10 11/16"; Height to Cold Inlet=21 5/16"; Height to Hot Outlet 400-1500gal=79 1/2"; Hot Outlet Angle=0.00°; Hot Outlet Extension=38 7/16"; Hot Outlet Radius=1 1/2"; Hot Outlet Side 400-1500gal NPT=0"; Hot Outlet Side Extension=38 7/16"; Hot Outlet Top 250-400gal NPT=3"; Input=1300000 Btu/h; Model=130 L 1250A-TPX; Pump Extension=41 13/16"; Pump Line Radius=1"; Pump Line to Economizer Location=41 1/4"; Rear Cowling Extension=1"; Relief Angle 50-160 Prefix=51.38°; Relief Angle 75-160 Prefix=45.00°; Relief Extension=41 7/16"; Relief Extension 50-160 Prefix=41 7/16"; Relief Extension 75-160 Prefix=43 7/16"; Relief Height=78 1/4"; Relief NPT=3/4"; Relief Radius=3/8"; Shipping Weight lbs.=4180; Skid Length=111 1/2"; Skid Spacing=44"; Skid to Front=68 13/16"; Test Building Return Height=20 11/16"; Unit Height=94 1/8"; Unit Radius=37 7/16"; Vent Connection Housing Extension=8 13/16"; Vent Extension=40 13/16"; Vent Height=7 1/4"; Vent Location=4 11/16"
- 160 L 1250A-TPX: 100 Prefix Recovery Rate 40F to 140F (gph)=-; 130 Prefix Recovery Rate 40F to 140F (gph)=-; 160 Prefix Recovery Rate 40F to 140F (gph)=1880; 50 Prefix Recovery Rate 40F to 140F (gph)=-; 75 Prefix Recovery Rate 40F to 140F (gph)=-; Building Return Connection Height 50 (250-400gal only) prefix=1/2"; Building Return Connection Height 50-160 prefix=13 11/16"; Building Return Extension 250-400gal=1"; Building Return Extension 500-600gal=46 19/32"; Building Return Extension Angle 500-600gal=52.00°; Building Return Height=40"; Building Return Location=28 7/8"; Building Return NPT=2"; Building Return Radius=1"; Building Return to Economizer=15 3/16"; Burner Conn Height=89 1/8"; Burner Height=18 3/16"; Burner Housing -Y=18 7/16"; Burner Housing Extension=20"; Burner Housing to Left=7 1/4"; Burner Housing to Right=7 7/8"; Burner Nozzle Extension=12 3/8"; Cold Inlet Extension=43 3/4"; Cold Inlet NPT=3"; Cold Inlet Radius=1 1/2"; Combustion Air Connection X=15 7/16"; Combustion Air Connection to Right=3 9/16"; Condensate Extension=4 3/8"; Control Enclosure Angle=41.00°; Control Enclosure Location=41 5/16"; Control Panel Extension=44 7/16"; Drain Extension=39 1/16"; Drain NPT=1 1/2"; Drain Radius=3/4"; Economizer Connection Y=5 5/16"; Economizer Depth=10"; Economizer Inlet Outlet Connection Spacing=4"; Economizer Width=32"; Energy Height=33 11/16"; Flue Collector Extension=13 1/2"; Flue Collector Outlet to Front=6 5/8"; Flue Collector Radius=11 13/16"; Front Cowling Extension=47 1/2"; Gas Inlet NPT=1"; Gas Inlet Radius=1/2"; Gas Train Extension=19 3/8"; Gas Train To Front=11 5/8"; Gas Train Vertical=24"; Gas Train to Left=6 5/8"; Gas Train to Rear=10 11/16"; Height to Cold Inlet=21 5/16"; Height to Hot Outlet 400-1500gal=79 1/2"; Hot Outlet Angle=0.00°; Hot Outlet Extension=38 7/16"; Hot Outlet Radius=1 1/2"; Hot Outlet Side 400-1500gal NPT=0"; Hot Outlet Side Extension=38 7/16"; Hot Outlet Top 250-400gal NPT=3"; Input=1600000 Btu/h; Model=160 L 1250A-TPX; Pump Extension=41 13/16"; Pump Line Radius=1"; Pump Line to Economizer Location=41 1/4"; Rear Cowling Extension=1"; Relief Angle 50-160 Prefix=51.38°; Relief Angle 75-160 Prefix=45.00°; Relief Extension=41 7/16"; Relief Extension 50-160 Prefix=41 7/16"; Relief Extension 75-160 Prefix=43 7/16"; Relief Height=78 1/4"; Relief NPT=3/4"; Relief Radius=3/8"; Shipping Weight lbs.=4180; Skid Length=111 1/2"; Skid Spacing=44"; Skid to Front=65 13/16"; Test Building Return Height=20 11/16"; Unit Height=94 1/8"; Unit Radius=37 7/16"; Vent Connection Housing Extension=8 13/16"; Vent Extension=40 13/16"; Vent Height=7 1/4"; Vent Location=4 11/16"
- 50 L 1500A-TPX: 100 Prefix Recovery Rate 40F to 140F (gph)=-; 130 Prefix Recovery Rate 40F to 140F (gph)=-; 160 Prefix Recovery Rate 40F to 140F (gph)=-; 50 Prefix Recovery Rate 40F to 140F (gph)=587; 75 Prefix Recovery Rate 40F to 140F (gph)=-; Building Return Connection Height 50 (250-400gal only) prefix=1/2"; Building Return Connection Height 50-160 prefix=13 11/16"; Building Return Extension 250-400gal=1"; Building Return Extension 500-600gal=46 3/8"; Building Return Extension Angle 500-600gal=51.38°; Building Return Height=40"; Building Return Location=28 7/8"; Building Return NPT=1 1/2"; Building Return Radius=3/4"; Building Return to Economizer=13"; Burner Conn Height=101 1/8"; Burner Height=18 3/16"; Burner Housing -Y=15 5/8"; Burner Housing Extension=19"; Burner Housing to Left=5 3/16"; Burner Housing to Right=7 1/4"; Burner Nozzle Extension=12 3/8"; Cold Inlet Extension=43 5/16"; Cold Inlet NPT=3"; Cold Inlet Radius=1 1/2"; Combustion Air Connection X=15 7/16"; Combustion Air Connection to Right=3 9/16"; Condensate Extension=4 3/8"; Control Enclosure Angle=41.00°; Control Enclosure Location=41 5/16"; Control Panel Extension=44 7/16"; Drain Extension=39 1/16"; Drain NPT=1 1/2"; Drain Radius=3/4"; Economizer Connection Y=5 5/16"; Economizer Depth=10"; Economizer Inlet Outlet Connection Spacing=4"; Economizer Width=32"; Energy Height=33 11/16"; Flue Collector Extension=8 13/16"; Flue Collector Outlet to Front=3 11/16"; Flue Collector Radius=12 1/8"; Front Cowling Extension=47 7/16"; Gas Inlet NPT=1"; Gas Inlet Radius=1/2"; Gas Train Extension=17 3/8"; Gas Train To Front=10 11/16"; Gas Train Vertical=19 1/8"; Gas Train to Left=4 3/8"; Gas Train to Rear=10 1/8"; Height to Cold Inlet=21 5/16"; Height to Hot Outlet 400-1500gal=91 1/2"; Hot Outlet Angle=0.00°; Hot Outlet Extension=38 7/16"; Hot Outlet Radius=1 1/2"; Hot Outlet Side 400-1500gal NPT=0"; Hot Outlet Side Extension=38 7/16"; Hot Outlet Top 250-400gal NPT=3"; Input=500000 Btu/h; Model=50 L 1500A-TPX; Pump Extension=41 13/16"; Pump Line Radius=5/8"; Pump Line to Economizer Location=41 1/16"; Rear Cowling Extension=1"; Relief Angle 50-160 Prefix=51.38°; Relief Angle 75-160 Prefix=45.00°; Relief Extension=41 7/16"; Relief Extension 50-160 Prefix=41 7/16"; Relief Extension 75-160 Prefix=10"; Relief Height=90 1/4"; Relief NPT=3/4"; Relief Radius=3/8"; Shipping Weight lbs.=4045; Skid Length=104"; Skid Spacing=44"; Skid to Front=61 9/16"; Test Building Return Height=20 11/16"; Unit Height=106 1/8"; Unit Radius=37 7/16"; Vent Connection Housing Extension=8 13/16"; Vent Extension=40 13/16"; Vent Height=6 7/8"; Vent Location=4"
- 75 L 1500A-TPX: 100 Prefix Recovery Rate 40F to 140F (gph)=-; 130 Prefix Recovery Rate 40F to 140F (gph)=-; 160 Prefix Recovery Rate 40F to 140F (gph)=-; 50 Prefix Recovery Rate 40F to 140F (gph)=-; 75 Prefix Recovery Rate 40F to 140F (gph)=881; Building Return Connection Height 50 (250-400gal only) prefix=1/2"; Building Return Connection Height 50-160 prefix=13 11/16"; Building Return Extension 250-400gal=1"; Building Return Extension 500-600gal=46 3/8"; Building Return Extension Angle 500-600gal=51.38°; Building Return Height=40"; Building Return Location=28 7/8"; Building Return NPT=1 1/2"; Building Return Radius=3/4"; Building Return to Economizer=13"; Burner Conn Height=101 1/8"; Burner Height=18 3/16"; Burner Housing -Y=18 7/16"; Burner Housing Extension=20"; Burner Housing to Left=7 1/4"; Burner Housing to Right=7 7/8"; Burner Nozzle Extension=12 3/8"; Cold Inlet Extension=43 5/16"; Cold Inlet NPT=3"; Cold Inlet Radius=1 1/2"; Combustion Air Connection X=15 7/16"; Combustion Air Connection to Right=3 9/16"; Condensate Extension=4 3/8"; Control Enclosure Angle=41.00°; Control Enclosure Location=41 5/16"; Control Panel Extension=44 7/16"; Drain Extension=39 1/16"; Drain NPT=1 1/2"; Drain Radius=3/4"; Economizer Connection Y=5 5/16"; Economizer Depth=10"; Economizer Inlet Outlet Connection Spacing=4"; Economizer Width=32"; Energy Height=33 11/16"; Flue Collector Extension=8 13/16"; Flue Collector Outlet to Front=3 11/16"; Flue Collector Radius=12 1/8"; Front Cowling Extension=47 7/16"; Gas Inlet NPT=1"; Gas Inlet Radius=1/2"; Gas Train Extension=17 3/8"; Gas Train To Front=11 5/8"; Gas Train Vertical=20 5/8"; Gas Train to Left=4 3/8"; Gas Train to Rear=10 11/16"; Height to Cold Inlet=21 5/16"; Height to Hot Outlet 400-1500gal=91 1/2"; Hot Outlet Angle=0.00°; Hot Outlet Extension=38 7/16"; Hot Outlet Radius=1 1/2"; Hot Outlet Side 400-1500gal NPT=0"; Hot Outlet Side Extension=38 7/16"; Hot Outlet Top 250-400gal NPT=3"; Input=750000 Btu/h; Model=75 L 1500A-TPX; Pump Extension=41 13/16"; Pump Line Radius=5/8"; Pump Line to Economizer Location=41 1/16"; Rear Cowling Extension=1"; Relief Angle 50-160 Prefix=51.38°; Relief Angle 75-160 Prefix=45.00°; Relief Extension=41 7/16"; Relief Extension 50-160 Prefix=41 7/16"; Relief Extension 75-160 Prefix=43 7/16"; Relief Height=90 1/4"; Relief NPT=3/4"; Relief Radius=3/8"; Shipping Weight lbs.=4125; Skid Length=104"; Skid Spacing=44"; Skid to Front=61 9/16"; Test Building Return Height=20 11/16"; Unit Height=106 1/8"; Unit Radius=37 7/16"; Vent Connection Housing Extension=8 13/16"; Vent Extension=40 13/16"; Vent Height=6 7/8"; Vent Location=4"
- 100 L 1500A-TPX: 100 Prefix Recovery Rate 40F to 140F (gph)=1175; 130 Prefix Recovery Rate 40F to 140F (gph)=-; 160 Prefix Recovery Rate 40F to 140F (gph)=-; 50 Prefix Recovery Rate 40F to 140F (gph)=-; 75 Prefix Recovery Rate 40F to 140F (gph)=-; Building Return Connection Height 50 (250-400gal only) prefix=1/2"; Building Return Connection Height 50-160 prefix=13 11/16"; Building Return Extension 250-400gal=1"; Building Return Extension 500-600gal=46 3/8"; Building Return Extension Angle 500-600gal=51.38°; Building Return Height=40"; Building Return Location=28 7/8"; Building Return NPT=1 1/2"; Building Return Radius=3/4"; Building Return to Economizer=13"; Burner Conn Height=101 1/8"; Burner Height=18 3/16"; Burner Housing -Y=18 7/16"; Burner Housing Extension=20"; Burner Housing to Left=7 1/4"; Burner Housing to Right=7 7/8"; Burner Nozzle Extension=12 3/8"; Cold Inlet Extension=43 5/16"; Cold Inlet NPT=3"; Cold Inlet Radius=1 1/2"; Combustion Air Connection X=15 7/16"; Combustion Air Connection to Right=3 9/16"; Condensate Extension=4 3/8"; Control Enclosure Angle=41.00°; Control Enclosure Location=41 5/16"; Control Panel Extension=44 7/16"; Drain Extension=39 1/16"; Drain NPT=1 1/2"; Drain Radius=3/4"; Economizer Connection Y=5 5/16"; Economizer Depth=10"; Economizer Inlet Outlet Connection Spacing=4"; Economizer Width=32"; Energy Height=33 11/16"; Flue Collector Extension=8 13/16"; Flue Collector Outlet to Front=3 11/16"; Flue Collector Radius=12 1/8"; Front Cowling Extension=47 7/16"; Gas Inlet NPT=1"; Gas Inlet Radius=1/2"; Gas Train Extension=17 3/8"; Gas Train To Front=11 5/8"; Gas Train Vertical=20 5/8"; Gas Train to Left=4 3/8"; Gas Train to Rear=10 11/16"; Height to Cold Inlet=21 5/16"; Height to Hot Outlet 400-1500gal=91 1/2"; Hot Outlet Angle=45.00°; Hot Outlet Extension=38 7/16"; Hot Outlet Radius=1 1/2"; Hot Outlet Side 400-1500gal NPT=0"; Hot Outlet Side Extension=38 7/16"; Hot Outlet Top 250-400gal NPT=3"; Input=1000000 Btu/h; Model=100 L 1500A-TPX; Pump Extension=41 13/16"; Pump Line Radius=5/8"; Pump Line to Economizer Location=41 1/16"; Rear Cowling Extension=1"; Relief Angle 50-160 Prefix=51.38°; Relief Angle 75-160 Prefix=45.00°; Relief Extension=41 7/16"; Relief Extension 50-160 Prefix=41 7/16"; Relief Extension 75-160 Prefix=43 7/16"; Relief Height=90 1/4"; Relief NPT=3/4"; Relief Radius=3/8"; Shipping Weight lbs.=4165; Skid Length=104"; Skid Spacing=44"; Skid to Front=61 9/16"; Test Building Return Height=20 11/16"; Unit Height=106 1/8"; Unit Radius=37 7/16"; Vent Connection Housing Extension=8 13/16"; Vent Extension=40 13/16"; Vent Height=6 7/8"; Vent Location=4"
- 130 L 1500A-TPX: 100 Prefix Recovery Rate 40F to 140F (gph)=-; 130 Prefix Recovery Rate 40F to 140F (gph)=1527; 160 Prefix Recovery Rate 40F to 140F (gph)=-; 50 Prefix Recovery Rate 40F to 140F (gph)=-; 75 Prefix Recovery Rate 40F to 140F (gph)=-; Building Return Connection Height 50 (250-400gal only) prefix=1/2"; Building Return Connection Height 50-160 prefix=13 11/16"; Building Return Extension 250-400gal=1"; Building Return Extension 500-600gal=46 19/32"; Building Return Extension Angle 500-600gal=52.00°; Building Return Height=40"; Building Return Location=28 7/8"; Building Return NPT=2"; Building Return Radius=1"; Building Return to Economizer=15 3/16"; Burner Conn Height=101 1/8"; Burner Height=18 3/16"; Burner Housing -Y=18 7/16"; Burner Housing Extension=20"; Burner Housing to Left=7 1/4"; Burner Housing to Right=7 7/8"; Burner Nozzle Extension=12 3/8"; Cold Inlet Extension=43 3/4"; Cold Inlet NPT=3"; Cold Inlet Radius=1 1/2"; Combustion Air Connection X=15 7/16"; Combustion Air Connection to Right=3 9/16"; Condensate Extension=4 3/8"; Control Enclosure Angle=41.00°; Control Enclosure Location=41 5/16"; Control Panel Extension=44 7/16"; Drain Extension=39 1/16"; Drain NPT=1 1/2"; Drain Radius=3/4"; Economizer Connection Y=5 5/16"; Economizer Depth=10"; Economizer Inlet Outlet Connection Spacing=4"; Economizer Width=32"; Energy Height=33 11/16"; Flue Collector Extension=13 1/2"; Flue Collector Outlet to Front=6 5/8"; Flue Collector Radius=11 13/16"; Front Cowling Extension=47 1/2"; Gas Inlet NPT=1"; Gas Inlet Radius=1/2"; Gas Train Extension=19 3/8"; Gas Train To Front=11 5/8"; Gas Train Vertical=24"; Gas Train to Left=6 5/8"; Gas Train to Rear=10 11/16"; Height to Cold Inlet=21 5/16"; Height to Hot Outlet 400-1500gal=91 1/2"; Hot Outlet Angle=0.00°; Hot Outlet Extension=38 7/16"; Hot Outlet Radius=1 1/2"; Hot Outlet Side 400-1500gal NPT=0"; Hot Outlet Side Extension=38 7/16"; Hot Outlet Top 250-400gal NPT=3"; Input=1300000 Btu/h; Model=130 L 1500A-TPX; Pump Extension=41 13/16"; Pump Line Radius=1"; Pump Line to Economizer Location=41 1/4"; Rear Cowling Extension=1"; Relief Angle 50-160 Prefix=51.38°; Relief Angle 75-160 Prefix=45.00°; Relief Extension=41 7/16"; Relief Extension 50-160 Prefix=41 7/16"; Relief Extension 75-160 Prefix=43 7/16"; Relief Height=90 1/4"; Relief NPT=3/4"; Relief Radius=3/8"; Shipping Weight lbs.=4395; Skid Length=111 1/2"; Skid Spacing=44"; Skid to Front=65 13/16"; Test Building Return Height=20 11/16"; Unit Height=106 1/8"; Unit Radius=37 7/16"; Vent Connection Housing Extension=8 13/16"; Vent Extension=40 13/16"; Vent Height=7 1/4"; Vent Location=4 11/16"
- 160 L 1500A-TPX: 100 Prefix Recovery Rate 40F to 140F (gph)=-; 130 Prefix Recovery Rate 40F to 140F (gph)=-; 160 Prefix Recovery Rate 40F to 140F (gph)=1880; 50 Prefix Recovery Rate 40F to 140F (gph)=-; 75 Prefix Recovery Rate 40F to 140F (gph)=-; Building Return Connection Height 50 (250-400gal only) prefix=1/2"; Building Return Connection Height 50-160 prefix=13 11/16"; Building Return Extension 250-400gal=1"; Building Return Extension 500-600gal=46 19/32"; Building Return Extension Angle 500-600gal=52.00°; Building Return Height=40"; Building Return Location=28 7/8"; Building Return NPT=2"; Building Return Radius=1"; Building Return to Economizer=15 3/16"; Burner Conn Height=101 1/8"; Burner Height=18 3/16"; Burner Housing -Y=18 7/16"; Burner Housing Extension=20"; Burner Housing to Left=7 1/4"; Burner Housing to Right=7 7/8"; Burner Nozzle Extension=12 3/8"; Cold Inlet Extension=43 3/4"; Cold Inlet NPT=3"; Cold Inlet Radius=1 1/2"; Combustion Air Connection X=15 7/16"; Combustion Air Connection to Right=3 9/16"; Condensate Extension=4 3/8"; Control Enclosure Angle=41.00°; Control Enclosure Location=41 5/16"; Control Panel Extension=44 7/16"; Drain Extension=39 1/16"; Drain NPT=1 1/2"; Drain Radius=3/4"; Economizer Connection Y=5 5/16"; Economizer Depth=10"; Economizer Inlet Outlet Connection Spacing=4"; Economizer Width=32"; Energy Height=33 11/16"; Flue Collector Extension=13 1/2"; Flue Collector Outlet to Front=6 5/8"; Flue Collector Radius=11 13/16"; Front Cowling Extension=47 1/2"; Gas Inlet NPT=1"; Gas Inlet Radius=1/2"; Gas Train Extension=19 3/8"; Gas Train To Front=11 5/8"; Gas Train Vertical=24"; Gas Train to Left=6 5/8"; Gas Train to Rear=10 11/16"; Height to Cold Inlet=21 5/16"; Height to Hot Outlet 400-1500gal=91 1/2"; Hot Outlet Angle=0.00°; Hot Outlet Extension=38 7/16"; Hot Outlet Radius=1 1/2"; Hot Outlet Side 400-1500gal NPT=0"; Hot Outlet Side Extension=38 7/16"; Hot Outlet Top 250-400gal NPT=3"; Input=1600000 Btu/h; Model=160 L 1500A-TPX; Pump Extension=41 13/16"; Pump Line Radius=1"; Pump Line to Economizer Location=41 1/4"; Rear Cowling Extension=1"; Relief Angle 50-160 Prefix=51.38°; Relief Angle 75-160 Prefix=45.00°; Relief Extension=41 7/16"; Relief Extension 50-160 Prefix=41 7/16"; Relief Extension 75-160 Prefix=43 7/16"; Relief Height=90 1/4"; Relief NPT=3/4"; Relief Radius=3/8"; Shipping Weight lbs.=4405; Skid Length=111 1/2"; Skid Spacing=44"; Skid to Front=68 13/16"; Test Building Return Height=20 11/16"; Unit Height=106 1/8"; Unit Radius=37 7/16"; Vent Connection Housing Extension=8 13/16"; Vent Extension=40 13/16"; Vent Height=7 1/4"; Vent Location=4 11/16"

## geometry (parser evidence)
native form markers: Sweep x2
no freeform markers — native parametric forms only
